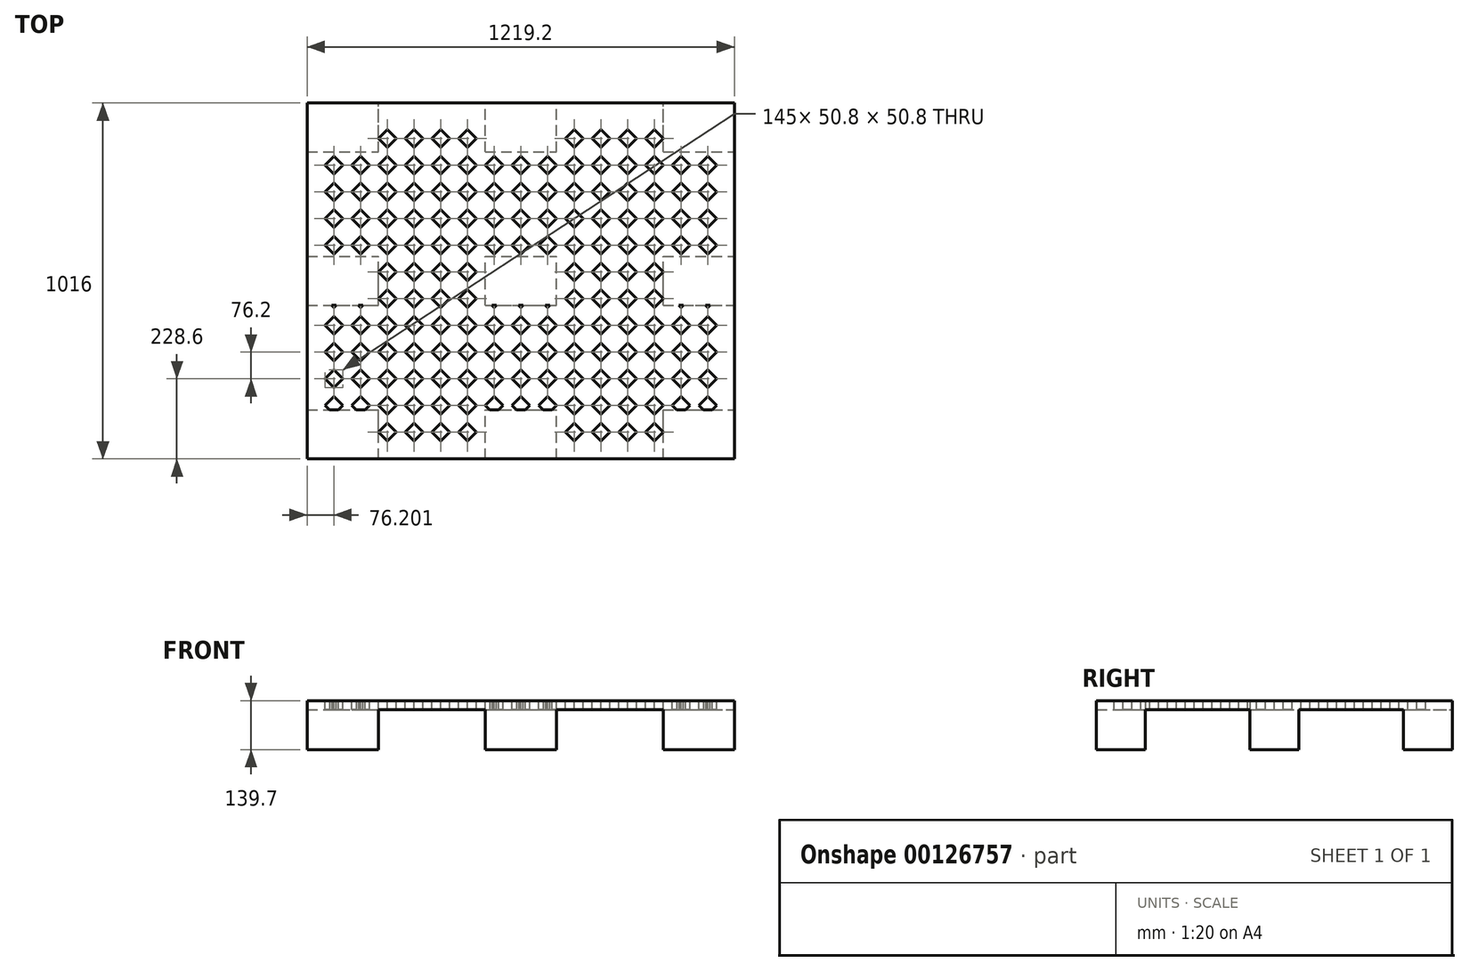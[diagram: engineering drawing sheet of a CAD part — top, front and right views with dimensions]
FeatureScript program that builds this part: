
annotation { "Feature Type Name" : "Feature", "Feature Type Description" : "" }
export const myFeature = defineFeature(function(context is Context, id is Id, definition is map)
    precondition{}
    {
        {
            var Q0;
            Q0=qCreatedBy(makeId("Top.planeOp"),FACE);
            var sketch = newSketch(context, id + "F0", { "sketchPlane" : qUnion([Q0])});
            skLineSegment(sketch, "E0.bottom", {"start": v(643.63, 508) * mm, "end": v(-575.57, 508) * mm});
            skLineSegment(sketch, "E0.top", {"start": v(643.63, -508) * mm, "end": v(-575.57, -508) * mm});
            skLineSegment(sketch, "E0.left", {"start": v(643.63, 508) * mm, "end": v(643.63, -508) * mm});
            skLineSegment(sketch, "E0.right", {"start": v(-575.57, 508) * mm, "end": v(-575.57, -508) * mm});
            skPoint(sketch, "E0.middle", {"position": v(34.03, 0) * mm});
            skSolve(sketch);
        }
        {
            var Q0;
            Q0 = qSketchRegion(id + "F0", true);
            extrude(context, id + "F1", {"entities" : qUnion([Q0]), "depth" : 25.4 * mm});
        }
        {
            var Q0;
            Q0=makeQuery(id+"F1.opExtrude","CAP_FACE",FACE,{"disambiguationData":[OSD([sQuery(id+"F0.wireOp",EDGE,"E0.bottom"),sQuery(id+"F0.wireOp",EDGE,"E0.top"),sQuery(id+"F0.wireOp",EDGE,"E0.left"),sQuery(id+"F0.wireOp",EDGE,"E0.right")])],"isStart":false});
            var sketch = newSketch(context, id + "F2", { "sketchPlane" : qUnion([Q0])});
            skLineSegment(sketch, "E1.bottom", {"start": v(-575.57, -508) * mm, "end": v(-524.77, -508) * mm, "construction": true});
            skLineSegment(sketch, "E1.top", {"start": v(-575.57, -457.2) * mm, "end": v(-524.77, -457.2) * mm, "construction": true});
            skLineSegment(sketch, "E1.left", {"start": v(-575.57, -508) * mm, "end": v(-575.57, -457.2) * mm, "construction": true});
            skLineSegment(sketch, "E1.right", {"start": v(-524.77, -508) * mm, "end": v(-524.77, -457.2) * mm, "construction": true});
            skLineSegment(sketch, "E2.bottom", {"start": v(-524.77, -457.2) * mm, "end": v(-473.97, -457.2) * mm, "construction": true});
            skLineSegment(sketch, "E2.top", {"start": v(-524.77, -406.4) * mm, "end": v(-473.97, -406.4) * mm, "construction": true});
            skLineSegment(sketch, "E2.left", {"start": v(-524.77, -457.2) * mm, "end": v(-524.77, -406.4) * mm, "construction": true});
            skLineSegment(sketch, "E2.right", {"start": v(-473.97, -457.2) * mm, "end": v(-473.97, -406.4) * mm, "construction": true});
            skLineSegment(sketch, "E3", {"start": v(-524.77, -431.8) * mm, "end": v(-499.37, -406.4) * mm});
            skLineSegment(sketch, "E4", {"start": v(-499.37, -406.4) * mm, "end": v(-473.97, -431.8) * mm});
            skLineSegment(sketch, "E5", {"start": v(-473.97, -431.8) * mm, "end": v(-499.37, -457.2) * mm});
            skLineSegment(sketch, "E6", {"start": v(-499.37, -457.2) * mm, "end": v(-524.77, -431.8) * mm});
            skLineSegment(sketch, "E7.0.1.0", {"start": v(-499.37, -330.2) * mm, "end": v(-473.97, -355.6) * mm});
            skLineSegment(sketch, "E7.0.1.1", {"start": v(-524.77, -355.6) * mm, "end": v(-499.37, -330.2) * mm});
            skLineSegment(sketch, "E7.0.1.2", {"start": v(-499.37, -381) * mm, "end": v(-524.77, -355.6) * mm});
            skLineSegment(sketch, "E7.0.1.3", {"start": v(-473.97, -355.6) * mm, "end": v(-499.37, -381) * mm});
            skLineSegment(sketch, "E7.0.2.0", {"start": v(-499.37, -254) * mm, "end": v(-473.97, -279.4) * mm});
            skLineSegment(sketch, "E7.0.2.1", {"start": v(-524.77, -279.4) * mm, "end": v(-499.37, -254) * mm});
            skLineSegment(sketch, "E7.0.2.2", {"start": v(-499.37, -304.8) * mm, "end": v(-524.77, -279.4) * mm});
            skLineSegment(sketch, "E7.0.2.3", {"start": v(-473.97, -279.4) * mm, "end": v(-499.37, -304.8) * mm});
            skLineSegment(sketch, "E7.0.3.0", {"start": v(-499.37, -177.8) * mm, "end": v(-473.97, -203.2) * mm});
            skLineSegment(sketch, "E7.0.3.1", {"start": v(-524.77, -203.2) * mm, "end": v(-499.37, -177.8) * mm});
            skLineSegment(sketch, "E7.0.3.2", {"start": v(-499.37, -228.6) * mm, "end": v(-524.77, -203.2) * mm});
            skLineSegment(sketch, "E7.0.3.3", {"start": v(-473.97, -203.2) * mm, "end": v(-499.37, -228.6) * mm});
            skLineSegment(sketch, "E7.0.4.0", {"start": v(-499.37, -101.6) * mm, "end": v(-473.97, -127) * mm});
            skLineSegment(sketch, "E7.0.4.1", {"start": v(-524.77, -127) * mm, "end": v(-499.37, -101.6) * mm});
            skLineSegment(sketch, "E7.0.4.2", {"start": v(-499.37, -152.4) * mm, "end": v(-524.77, -127) * mm});
            skLineSegment(sketch, "E7.0.4.3", {"start": v(-473.97, -127) * mm, "end": v(-499.37, -152.4) * mm});
            skLineSegment(sketch, "E7.0.5.0", {"start": v(-499.37, -25.4) * mm, "end": v(-473.97, -50.8) * mm});
            skLineSegment(sketch, "E7.0.5.1", {"start": v(-524.77, -50.8) * mm, "end": v(-499.37, -25.4) * mm});
            skLineSegment(sketch, "E7.0.5.2", {"start": v(-499.37, -76.2) * mm, "end": v(-524.77, -50.8) * mm});
            skLineSegment(sketch, "E7.0.5.3", {"start": v(-473.97, -50.8) * mm, "end": v(-499.37, -76.2) * mm});
            skLineSegment(sketch, "E7.0.6.0", {"start": v(-499.37, 50.8) * mm, "end": v(-473.97, 25.4) * mm});
            skLineSegment(sketch, "E7.0.6.1", {"start": v(-524.77, 25.4) * mm, "end": v(-499.37, 50.8) * mm});
            skLineSegment(sketch, "E7.0.6.2", {"start": v(-499.37, 0) * mm, "end": v(-524.77, 25.4) * mm});
            skLineSegment(sketch, "E7.0.6.3", {"start": v(-473.97, 25.4) * mm, "end": v(-499.37, 0) * mm});
            skLineSegment(sketch, "E7.0.7.0", {"start": v(-499.37, 127) * mm, "end": v(-473.97, 101.6) * mm});
            skLineSegment(sketch, "E7.0.7.1", {"start": v(-524.77, 101.6) * mm, "end": v(-499.37, 127) * mm});
            skLineSegment(sketch, "E7.0.7.2", {"start": v(-499.37, 76.2) * mm, "end": v(-524.77, 101.6) * mm});
            skLineSegment(sketch, "E7.0.7.3", {"start": v(-473.97, 101.6) * mm, "end": v(-499.37, 76.2) * mm});
            skLineSegment(sketch, "E7.0.8.0", {"start": v(-499.37, 203.2) * mm, "end": v(-473.97, 177.8) * mm});
            skLineSegment(sketch, "E7.0.8.1", {"start": v(-524.77, 177.8) * mm, "end": v(-499.37, 203.2) * mm});
            skLineSegment(sketch, "E7.0.8.2", {"start": v(-499.37, 152.4) * mm, "end": v(-524.77, 177.8) * mm});
            skLineSegment(sketch, "E7.0.8.3", {"start": v(-473.97, 177.8) * mm, "end": v(-499.37, 152.4) * mm});
            skLineSegment(sketch, "E7.0.9.0", {"start": v(-499.37, 279.4) * mm, "end": v(-473.97, 254) * mm});
            skLineSegment(sketch, "E7.0.9.1", {"start": v(-524.77, 254) * mm, "end": v(-499.37, 279.4) * mm});
            skLineSegment(sketch, "E7.0.9.2", {"start": v(-499.37, 228.6) * mm, "end": v(-524.77, 254) * mm});
            skLineSegment(sketch, "E7.0.9.3", {"start": v(-473.97, 254) * mm, "end": v(-499.37, 228.6) * mm});
            skLineSegment(sketch, "E7.0.10.0", {"start": v(-499.37, 355.6) * mm, "end": v(-473.97, 330.2) * mm});
            skLineSegment(sketch, "E7.0.10.1", {"start": v(-524.77, 330.2) * mm, "end": v(-499.37, 355.6) * mm});
            skLineSegment(sketch, "E7.0.10.2", {"start": v(-499.37, 304.8) * mm, "end": v(-524.77, 330.2) * mm});
            skLineSegment(sketch, "E7.0.10.3", {"start": v(-473.97, 330.2) * mm, "end": v(-499.37, 304.8) * mm});
            skLineSegment(sketch, "E7.0.11.0", {"start": v(-499.37, 431.8) * mm, "end": v(-473.97, 406.4) * mm});
            skLineSegment(sketch, "E7.0.11.1", {"start": v(-524.77, 406.4) * mm, "end": v(-499.37, 431.8) * mm});
            skLineSegment(sketch, "E7.0.11.2", {"start": v(-499.37, 381) * mm, "end": v(-524.77, 406.4) * mm});
            skLineSegment(sketch, "E7.0.11.3", {"start": v(-473.97, 406.4) * mm, "end": v(-499.37, 381) * mm});
            skLineSegment(sketch, "E7.1.0.0", {"start": v(-423.17, -406.4) * mm, "end": v(-397.77, -431.8) * mm});
            skLineSegment(sketch, "E7.1.0.1", {"start": v(-448.57, -431.8) * mm, "end": v(-423.17, -406.4) * mm});
            skLineSegment(sketch, "E7.1.0.2", {"start": v(-423.17, -457.2) * mm, "end": v(-448.57, -431.8) * mm});
            skLineSegment(sketch, "E7.1.0.3", {"start": v(-397.77, -431.8) * mm, "end": v(-423.17, -457.2) * mm});
            skLineSegment(sketch, "E7.1.1.0", {"start": v(-423.17, -330.2) * mm, "end": v(-397.77, -355.6) * mm});
            skLineSegment(sketch, "E7.1.1.1", {"start": v(-448.57, -355.6) * mm, "end": v(-423.17, -330.2) * mm});
            skLineSegment(sketch, "E7.1.1.2", {"start": v(-423.17, -381) * mm, "end": v(-448.57, -355.6) * mm});
            skLineSegment(sketch, "E7.1.1.3", {"start": v(-397.77, -355.6) * mm, "end": v(-423.17, -381) * mm});
            skLineSegment(sketch, "E7.1.2.0", {"start": v(-423.17, -254) * mm, "end": v(-397.77, -279.4) * mm});
            skLineSegment(sketch, "E7.1.2.1", {"start": v(-448.57, -279.4) * mm, "end": v(-423.17, -254) * mm});
            skLineSegment(sketch, "E7.1.2.2", {"start": v(-423.17, -304.8) * mm, "end": v(-448.57, -279.4) * mm});
            skLineSegment(sketch, "E7.1.2.3", {"start": v(-397.77, -279.4) * mm, "end": v(-423.17, -304.8) * mm});
            skLineSegment(sketch, "E7.1.3.0", {"start": v(-423.17, -177.8) * mm, "end": v(-397.77, -203.2) * mm});
            skLineSegment(sketch, "E7.1.3.1", {"start": v(-448.57, -203.2) * mm, "end": v(-423.17, -177.8) * mm});
            skLineSegment(sketch, "E7.1.3.2", {"start": v(-423.17, -228.6) * mm, "end": v(-448.57, -203.2) * mm});
            skLineSegment(sketch, "E7.1.3.3", {"start": v(-397.77, -203.2) * mm, "end": v(-423.17, -228.6) * mm});
            skLineSegment(sketch, "E7.1.4.0", {"start": v(-423.17, -101.6) * mm, "end": v(-397.77, -127) * mm});
            skLineSegment(sketch, "E7.1.4.1", {"start": v(-448.57, -127) * mm, "end": v(-423.17, -101.6) * mm});
            skLineSegment(sketch, "E7.1.4.2", {"start": v(-423.17, -152.4) * mm, "end": v(-448.57, -127) * mm});
            skLineSegment(sketch, "E7.1.4.3", {"start": v(-397.77, -127) * mm, "end": v(-423.17, -152.4) * mm});
            skLineSegment(sketch, "E7.1.5.0", {"start": v(-423.17, -25.4) * mm, "end": v(-397.77, -50.8) * mm});
            skLineSegment(sketch, "E7.1.5.1", {"start": v(-448.57, -50.8) * mm, "end": v(-423.17, -25.4) * mm});
            skLineSegment(sketch, "E7.1.5.2", {"start": v(-423.17, -76.2) * mm, "end": v(-448.57, -50.8) * mm});
            skLineSegment(sketch, "E7.1.5.3", {"start": v(-397.77, -50.8) * mm, "end": v(-423.17, -76.2) * mm});
            skLineSegment(sketch, "E7.1.6.0", {"start": v(-423.17, 50.8) * mm, "end": v(-397.77, 25.4) * mm});
            skLineSegment(sketch, "E7.1.6.1", {"start": v(-448.57, 25.4) * mm, "end": v(-423.17, 50.8) * mm});
            skLineSegment(sketch, "E7.1.6.2", {"start": v(-423.17, 0) * mm, "end": v(-448.57, 25.4) * mm});
            skLineSegment(sketch, "E7.1.6.3", {"start": v(-397.77, 25.4) * mm, "end": v(-423.17, 0) * mm});
            skLineSegment(sketch, "E7.1.7.0", {"start": v(-423.17, 127) * mm, "end": v(-397.77, 101.6) * mm});
            skLineSegment(sketch, "E7.1.7.1", {"start": v(-448.57, 101.6) * mm, "end": v(-423.17, 127) * mm});
            skLineSegment(sketch, "E7.1.7.2", {"start": v(-423.17, 76.2) * mm, "end": v(-448.57, 101.6) * mm});
            skLineSegment(sketch, "E7.1.7.3", {"start": v(-397.77, 101.6) * mm, "end": v(-423.17, 76.2) * mm});
            skLineSegment(sketch, "E7.1.8.0", {"start": v(-423.17, 203.2) * mm, "end": v(-397.77, 177.8) * mm});
            skLineSegment(sketch, "E7.1.8.1", {"start": v(-448.57, 177.8) * mm, "end": v(-423.17, 203.2) * mm});
            skLineSegment(sketch, "E7.1.8.2", {"start": v(-423.17, 152.4) * mm, "end": v(-448.57, 177.8) * mm});
            skLineSegment(sketch, "E7.1.8.3", {"start": v(-397.77, 177.8) * mm, "end": v(-423.17, 152.4) * mm});
            skLineSegment(sketch, "E7.1.9.0", {"start": v(-423.17, 279.4) * mm, "end": v(-397.77, 254) * mm});
            skLineSegment(sketch, "E7.1.9.1", {"start": v(-448.57, 254) * mm, "end": v(-423.17, 279.4) * mm});
            skLineSegment(sketch, "E7.1.9.2", {"start": v(-423.17, 228.6) * mm, "end": v(-448.57, 254) * mm});
            skLineSegment(sketch, "E7.1.9.3", {"start": v(-397.77, 254) * mm, "end": v(-423.17, 228.6) * mm});
            skLineSegment(sketch, "E7.1.10.0", {"start": v(-423.17, 355.6) * mm, "end": v(-397.77, 330.2) * mm});
            skLineSegment(sketch, "E7.1.10.1", {"start": v(-448.57, 330.2) * mm, "end": v(-423.17, 355.6) * mm});
            skLineSegment(sketch, "E7.1.10.2", {"start": v(-423.17, 304.8) * mm, "end": v(-448.57, 330.2) * mm});
            skLineSegment(sketch, "E7.1.10.3", {"start": v(-397.77, 330.2) * mm, "end": v(-423.17, 304.8) * mm});
            skLineSegment(sketch, "E7.1.11.0", {"start": v(-423.17, 431.8) * mm, "end": v(-397.77, 406.4) * mm});
            skLineSegment(sketch, "E7.1.11.1", {"start": v(-448.57, 406.4) * mm, "end": v(-423.17, 431.8) * mm});
            skLineSegment(sketch, "E7.1.11.2", {"start": v(-423.17, 381) * mm, "end": v(-448.57, 406.4) * mm});
            skLineSegment(sketch, "E7.1.11.3", {"start": v(-397.77, 406.4) * mm, "end": v(-423.17, 381) * mm});
            skLineSegment(sketch, "E7.2.0.0", {"start": v(-346.97, -406.4) * mm, "end": v(-321.57, -431.8) * mm});
            skLineSegment(sketch, "E7.2.0.1", {"start": v(-372.37, -431.8) * mm, "end": v(-346.97, -406.4) * mm});
            skLineSegment(sketch, "E7.2.0.2", {"start": v(-346.97, -457.2) * mm, "end": v(-372.37, -431.8) * mm});
            skLineSegment(sketch, "E7.2.0.3", {"start": v(-321.57, -431.8) * mm, "end": v(-346.97, -457.2) * mm});
            skLineSegment(sketch, "E7.2.1.0", {"start": v(-346.97, -330.2) * mm, "end": v(-321.57, -355.6) * mm});
            skLineSegment(sketch, "E7.2.1.1", {"start": v(-372.37, -355.6) * mm, "end": v(-346.97, -330.2) * mm});
            skLineSegment(sketch, "E7.2.1.2", {"start": v(-346.97, -381) * mm, "end": v(-372.37, -355.6) * mm});
            skLineSegment(sketch, "E7.2.1.3", {"start": v(-321.57, -355.6) * mm, "end": v(-346.97, -381) * mm});
            skLineSegment(sketch, "E7.2.2.0", {"start": v(-346.97, -254) * mm, "end": v(-321.57, -279.4) * mm});
            skLineSegment(sketch, "E7.2.2.1", {"start": v(-372.37, -279.4) * mm, "end": v(-346.97, -254) * mm});
            skLineSegment(sketch, "E7.2.2.2", {"start": v(-346.97, -304.8) * mm, "end": v(-372.37, -279.4) * mm});
            skLineSegment(sketch, "E7.2.2.3", {"start": v(-321.57, -279.4) * mm, "end": v(-346.97, -304.8) * mm});
            skLineSegment(sketch, "E7.2.3.0", {"start": v(-346.97, -177.8) * mm, "end": v(-321.57, -203.2) * mm});
            skLineSegment(sketch, "E7.2.3.1", {"start": v(-372.37, -203.2) * mm, "end": v(-346.97, -177.8) * mm});
            skLineSegment(sketch, "E7.2.3.2", {"start": v(-346.97, -228.6) * mm, "end": v(-372.37, -203.2) * mm});
            skLineSegment(sketch, "E7.2.3.3", {"start": v(-321.57, -203.2) * mm, "end": v(-346.97, -228.6) * mm});
            skLineSegment(sketch, "E7.2.4.0", {"start": v(-346.97, -101.6) * mm, "end": v(-321.57, -127) * mm});
            skLineSegment(sketch, "E7.2.4.1", {"start": v(-372.37, -127) * mm, "end": v(-346.97, -101.6) * mm});
            skLineSegment(sketch, "E7.2.4.2", {"start": v(-346.97, -152.4) * mm, "end": v(-372.37, -127) * mm});
            skLineSegment(sketch, "E7.2.4.3", {"start": v(-321.57, -127) * mm, "end": v(-346.97, -152.4) * mm});
            skLineSegment(sketch, "E7.2.5.0", {"start": v(-346.97, -25.4) * mm, "end": v(-321.57, -50.8) * mm});
            skLineSegment(sketch, "E7.2.5.1", {"start": v(-372.37, -50.8) * mm, "end": v(-346.97, -25.4) * mm});
            skLineSegment(sketch, "E7.2.5.2", {"start": v(-346.97, -76.2) * mm, "end": v(-372.37, -50.8) * mm});
            skLineSegment(sketch, "E7.2.5.3", {"start": v(-321.57, -50.8) * mm, "end": v(-346.97, -76.2) * mm});
            skLineSegment(sketch, "E7.2.6.0", {"start": v(-346.97, 50.8) * mm, "end": v(-321.57, 25.4) * mm});
            skLineSegment(sketch, "E7.2.6.1", {"start": v(-372.37, 25.4) * mm, "end": v(-346.97, 50.8) * mm});
            skLineSegment(sketch, "E7.2.6.2", {"start": v(-346.97, 0) * mm, "end": v(-372.37, 25.4) * mm});
            skLineSegment(sketch, "E7.2.6.3", {"start": v(-321.57, 25.4) * mm, "end": v(-346.97, 0) * mm});
            skLineSegment(sketch, "E7.2.7.0", {"start": v(-346.97, 127) * mm, "end": v(-321.57, 101.6) * mm});
            skLineSegment(sketch, "E7.2.7.1", {"start": v(-372.37, 101.6) * mm, "end": v(-346.97, 127) * mm});
            skLineSegment(sketch, "E7.2.7.2", {"start": v(-346.97, 76.2) * mm, "end": v(-372.37, 101.6) * mm});
            skLineSegment(sketch, "E7.2.7.3", {"start": v(-321.57, 101.6) * mm, "end": v(-346.97, 76.2) * mm});
            skLineSegment(sketch, "E7.2.8.0", {"start": v(-346.97, 203.2) * mm, "end": v(-321.57, 177.8) * mm});
            skLineSegment(sketch, "E7.2.8.1", {"start": v(-372.37, 177.8) * mm, "end": v(-346.97, 203.2) * mm});
            skLineSegment(sketch, "E7.2.8.2", {"start": v(-346.97, 152.4) * mm, "end": v(-372.37, 177.8) * mm});
            skLineSegment(sketch, "E7.2.8.3", {"start": v(-321.57, 177.8) * mm, "end": v(-346.97, 152.4) * mm});
            skLineSegment(sketch, "E7.2.9.0", {"start": v(-346.97, 279.4) * mm, "end": v(-321.57, 254) * mm});
            skLineSegment(sketch, "E7.2.9.1", {"start": v(-372.37, 254) * mm, "end": v(-346.97, 279.4) * mm});
            skLineSegment(sketch, "E7.2.9.2", {"start": v(-346.97, 228.6) * mm, "end": v(-372.37, 254) * mm});
            skLineSegment(sketch, "E7.2.9.3", {"start": v(-321.57, 254) * mm, "end": v(-346.97, 228.6) * mm});
            skLineSegment(sketch, "E7.2.10.0", {"start": v(-346.97, 355.6) * mm, "end": v(-321.57, 330.2) * mm});
            skLineSegment(sketch, "E7.2.10.1", {"start": v(-372.37, 330.2) * mm, "end": v(-346.97, 355.6) * mm});
            skLineSegment(sketch, "E7.2.10.2", {"start": v(-346.97, 304.8) * mm, "end": v(-372.37, 330.2) * mm});
            skLineSegment(sketch, "E7.2.10.3", {"start": v(-321.57, 330.2) * mm, "end": v(-346.97, 304.8) * mm});
            skLineSegment(sketch, "E7.2.11.0", {"start": v(-346.97, 431.8) * mm, "end": v(-321.57, 406.4) * mm});
            skLineSegment(sketch, "E7.2.11.1", {"start": v(-372.37, 406.4) * mm, "end": v(-346.97, 431.8) * mm});
            skLineSegment(sketch, "E7.2.11.2", {"start": v(-346.97, 381) * mm, "end": v(-372.37, 406.4) * mm});
            skLineSegment(sketch, "E7.2.11.3", {"start": v(-321.57, 406.4) * mm, "end": v(-346.97, 381) * mm});
            skLineSegment(sketch, "E7.3.0.0", {"start": v(-270.77, -406.4) * mm, "end": v(-245.37, -431.8) * mm});
            skLineSegment(sketch, "E7.3.0.1", {"start": v(-296.17, -431.8) * mm, "end": v(-270.77, -406.4) * mm});
            skLineSegment(sketch, "E7.3.0.2", {"start": v(-270.77, -457.2) * mm, "end": v(-296.17, -431.8) * mm});
            skLineSegment(sketch, "E7.3.0.3", {"start": v(-245.37, -431.8) * mm, "end": v(-270.77, -457.2) * mm});
            skLineSegment(sketch, "E7.3.1.0", {"start": v(-270.77, -330.2) * mm, "end": v(-245.37, -355.6) * mm});
            skLineSegment(sketch, "E7.3.1.1", {"start": v(-296.17, -355.6) * mm, "end": v(-270.77, -330.2) * mm});
            skLineSegment(sketch, "E7.3.1.2", {"start": v(-270.77, -381) * mm, "end": v(-296.17, -355.6) * mm});
            skLineSegment(sketch, "E7.3.1.3", {"start": v(-245.37, -355.6) * mm, "end": v(-270.77, -381) * mm});
            skLineSegment(sketch, "E7.3.2.0", {"start": v(-270.77, -254) * mm, "end": v(-245.37, -279.4) * mm});
            skLineSegment(sketch, "E7.3.2.1", {"start": v(-296.17, -279.4) * mm, "end": v(-270.77, -254) * mm});
            skLineSegment(sketch, "E7.3.2.2", {"start": v(-270.77, -304.8) * mm, "end": v(-296.17, -279.4) * mm});
            skLineSegment(sketch, "E7.3.2.3", {"start": v(-245.37, -279.4) * mm, "end": v(-270.77, -304.8) * mm});
            skLineSegment(sketch, "E7.3.3.0", {"start": v(-270.77, -177.8) * mm, "end": v(-245.37, -203.2) * mm});
            skLineSegment(sketch, "E7.3.3.1", {"start": v(-296.17, -203.2) * mm, "end": v(-270.77, -177.8) * mm});
            skLineSegment(sketch, "E7.3.3.2", {"start": v(-270.77, -228.6) * mm, "end": v(-296.17, -203.2) * mm});
            skLineSegment(sketch, "E7.3.3.3", {"start": v(-245.37, -203.2) * mm, "end": v(-270.77, -228.6) * mm});
            skLineSegment(sketch, "E7.3.4.0", {"start": v(-270.77, -101.6) * mm, "end": v(-245.37, -127) * mm});
            skLineSegment(sketch, "E7.3.4.1", {"start": v(-296.17, -127) * mm, "end": v(-270.77, -101.6) * mm});
            skLineSegment(sketch, "E7.3.4.2", {"start": v(-270.77, -152.4) * mm, "end": v(-296.17, -127) * mm});
            skLineSegment(sketch, "E7.3.4.3", {"start": v(-245.37, -127) * mm, "end": v(-270.77, -152.4) * mm});
            skLineSegment(sketch, "E7.3.5.0", {"start": v(-270.77, -25.4) * mm, "end": v(-245.37, -50.8) * mm});
            skLineSegment(sketch, "E7.3.5.1", {"start": v(-296.17, -50.8) * mm, "end": v(-270.77, -25.4) * mm});
            skLineSegment(sketch, "E7.3.5.2", {"start": v(-270.77, -76.2) * mm, "end": v(-296.17, -50.8) * mm});
            skLineSegment(sketch, "E7.3.5.3", {"start": v(-245.37, -50.8) * mm, "end": v(-270.77, -76.2) * mm});
            skLineSegment(sketch, "E7.3.6.0", {"start": v(-270.77, 50.8) * mm, "end": v(-245.37, 25.4) * mm});
            skLineSegment(sketch, "E7.3.6.1", {"start": v(-296.17, 25.4) * mm, "end": v(-270.77, 50.8) * mm});
            skLineSegment(sketch, "E7.3.6.2", {"start": v(-270.77, 0) * mm, "end": v(-296.17, 25.4) * mm});
            skLineSegment(sketch, "E7.3.6.3", {"start": v(-245.37, 25.4) * mm, "end": v(-270.77, 0) * mm});
            skLineSegment(sketch, "E7.3.7.0", {"start": v(-270.77, 127) * mm, "end": v(-245.37, 101.6) * mm});
            skLineSegment(sketch, "E7.3.7.1", {"start": v(-296.17, 101.6) * mm, "end": v(-270.77, 127) * mm});
            skLineSegment(sketch, "E7.3.7.2", {"start": v(-270.77, 76.2) * mm, "end": v(-296.17, 101.6) * mm});
            skLineSegment(sketch, "E7.3.7.3", {"start": v(-245.37, 101.6) * mm, "end": v(-270.77, 76.2) * mm});
            skLineSegment(sketch, "E7.3.8.0", {"start": v(-270.77, 203.2) * mm, "end": v(-245.37, 177.8) * mm});
            skLineSegment(sketch, "E7.3.8.1", {"start": v(-296.17, 177.8) * mm, "end": v(-270.77, 203.2) * mm});
            skLineSegment(sketch, "E7.3.8.2", {"start": v(-270.77, 152.4) * mm, "end": v(-296.17, 177.8) * mm});
            skLineSegment(sketch, "E7.3.8.3", {"start": v(-245.37, 177.8) * mm, "end": v(-270.77, 152.4) * mm});
            skLineSegment(sketch, "E7.3.9.0", {"start": v(-270.77, 279.4) * mm, "end": v(-245.37, 254) * mm});
            skLineSegment(sketch, "E7.3.9.1", {"start": v(-296.17, 254) * mm, "end": v(-270.77, 279.4) * mm});
            skLineSegment(sketch, "E7.3.9.2", {"start": v(-270.77, 228.6) * mm, "end": v(-296.17, 254) * mm});
            skLineSegment(sketch, "E7.3.9.3", {"start": v(-245.37, 254) * mm, "end": v(-270.77, 228.6) * mm});
            skLineSegment(sketch, "E7.3.10.0", {"start": v(-270.77, 355.6) * mm, "end": v(-245.37, 330.2) * mm});
            skLineSegment(sketch, "E7.3.10.1", {"start": v(-296.17, 330.2) * mm, "end": v(-270.77, 355.6) * mm});
            skLineSegment(sketch, "E7.3.10.2", {"start": v(-270.77, 304.8) * mm, "end": v(-296.17, 330.2) * mm});
            skLineSegment(sketch, "E7.3.10.3", {"start": v(-245.37, 330.2) * mm, "end": v(-270.77, 304.8) * mm});
            skLineSegment(sketch, "E7.3.11.0", {"start": v(-270.77, 431.8) * mm, "end": v(-245.37, 406.4) * mm});
            skLineSegment(sketch, "E7.3.11.1", {"start": v(-296.17, 406.4) * mm, "end": v(-270.77, 431.8) * mm});
            skLineSegment(sketch, "E7.3.11.2", {"start": v(-270.77, 381) * mm, "end": v(-296.17, 406.4) * mm});
            skLineSegment(sketch, "E7.3.11.3", {"start": v(-245.37, 406.4) * mm, "end": v(-270.77, 381) * mm});
            skLineSegment(sketch, "E7.4.0.0", {"start": v(-194.57, -406.4) * mm, "end": v(-169.17, -431.8) * mm});
            skLineSegment(sketch, "E7.4.0.1", {"start": v(-219.97, -431.8) * mm, "end": v(-194.57, -406.4) * mm});
            skLineSegment(sketch, "E7.4.0.2", {"start": v(-194.57, -457.2) * mm, "end": v(-219.97, -431.8) * mm});
            skLineSegment(sketch, "E7.4.0.3", {"start": v(-169.17, -431.8) * mm, "end": v(-194.57, -457.2) * mm});
            skLineSegment(sketch, "E7.4.1.0", {"start": v(-194.57, -330.2) * mm, "end": v(-169.17, -355.6) * mm});
            skLineSegment(sketch, "E7.4.1.1", {"start": v(-219.97, -355.6) * mm, "end": v(-194.57, -330.2) * mm});
            skLineSegment(sketch, "E7.4.1.2", {"start": v(-194.57, -381) * mm, "end": v(-219.97, -355.6) * mm});
            skLineSegment(sketch, "E7.4.1.3", {"start": v(-169.17, -355.6) * mm, "end": v(-194.57, -381) * mm});
            skLineSegment(sketch, "E7.4.2.0", {"start": v(-194.57, -254) * mm, "end": v(-169.17, -279.4) * mm});
            skLineSegment(sketch, "E7.4.2.1", {"start": v(-219.97, -279.4) * mm, "end": v(-194.57, -254) * mm});
            skLineSegment(sketch, "E7.4.2.2", {"start": v(-194.57, -304.8) * mm, "end": v(-219.97, -279.4) * mm});
            skLineSegment(sketch, "E7.4.2.3", {"start": v(-169.17, -279.4) * mm, "end": v(-194.57, -304.8) * mm});
            skLineSegment(sketch, "E7.4.3.0", {"start": v(-194.57, -177.8) * mm, "end": v(-169.17, -203.2) * mm});
            skLineSegment(sketch, "E7.4.3.1", {"start": v(-219.97, -203.2) * mm, "end": v(-194.57, -177.8) * mm});
            skLineSegment(sketch, "E7.4.3.2", {"start": v(-194.57, -228.6) * mm, "end": v(-219.97, -203.2) * mm});
            skLineSegment(sketch, "E7.4.3.3", {"start": v(-169.17, -203.2) * mm, "end": v(-194.57, -228.6) * mm});
            skLineSegment(sketch, "E7.4.4.0", {"start": v(-194.57, -101.6) * mm, "end": v(-169.17, -127) * mm});
            skLineSegment(sketch, "E7.4.4.1", {"start": v(-219.97, -127) * mm, "end": v(-194.57, -101.6) * mm});
            skLineSegment(sketch, "E7.4.4.2", {"start": v(-194.57, -152.4) * mm, "end": v(-219.97, -127) * mm});
            skLineSegment(sketch, "E7.4.4.3", {"start": v(-169.17, -127) * mm, "end": v(-194.57, -152.4) * mm});
            skLineSegment(sketch, "E7.4.5.0", {"start": v(-194.57, -25.4) * mm, "end": v(-169.17, -50.8) * mm});
            skLineSegment(sketch, "E7.4.5.1", {"start": v(-219.97, -50.8) * mm, "end": v(-194.57, -25.4) * mm});
            skLineSegment(sketch, "E7.4.5.2", {"start": v(-194.57, -76.2) * mm, "end": v(-219.97, -50.8) * mm});
            skLineSegment(sketch, "E7.4.5.3", {"start": v(-169.17, -50.8) * mm, "end": v(-194.57, -76.2) * mm});
            skLineSegment(sketch, "E7.4.6.0", {"start": v(-194.57, 50.8) * mm, "end": v(-169.17, 25.4) * mm});
            skLineSegment(sketch, "E7.4.6.1", {"start": v(-219.97, 25.4) * mm, "end": v(-194.57, 50.8) * mm});
            skLineSegment(sketch, "E7.4.6.2", {"start": v(-194.57, 0) * mm, "end": v(-219.97, 25.4) * mm});
            skLineSegment(sketch, "E7.4.6.3", {"start": v(-169.17, 25.4) * mm, "end": v(-194.57, 0) * mm});
            skLineSegment(sketch, "E7.4.7.0", {"start": v(-194.57, 127) * mm, "end": v(-169.17, 101.6) * mm});
            skLineSegment(sketch, "E7.4.7.1", {"start": v(-219.97, 101.6) * mm, "end": v(-194.57, 127) * mm});
            skLineSegment(sketch, "E7.4.7.2", {"start": v(-194.57, 76.2) * mm, "end": v(-219.97, 101.6) * mm});
            skLineSegment(sketch, "E7.4.7.3", {"start": v(-169.17, 101.6) * mm, "end": v(-194.57, 76.2) * mm});
            skLineSegment(sketch, "E7.4.8.0", {"start": v(-194.57, 203.2) * mm, "end": v(-169.17, 177.8) * mm});
            skLineSegment(sketch, "E7.4.8.1", {"start": v(-219.97, 177.8) * mm, "end": v(-194.57, 203.2) * mm});
            skLineSegment(sketch, "E7.4.8.2", {"start": v(-194.57, 152.4) * mm, "end": v(-219.97, 177.8) * mm});
            skLineSegment(sketch, "E7.4.8.3", {"start": v(-169.17, 177.8) * mm, "end": v(-194.57, 152.4) * mm});
            skLineSegment(sketch, "E7.4.9.0", {"start": v(-194.57, 279.4) * mm, "end": v(-169.17, 254) * mm});
            skLineSegment(sketch, "E7.4.9.1", {"start": v(-219.97, 254) * mm, "end": v(-194.57, 279.4) * mm});
            skLineSegment(sketch, "E7.4.9.2", {"start": v(-194.57, 228.6) * mm, "end": v(-219.97, 254) * mm});
            skLineSegment(sketch, "E7.4.9.3", {"start": v(-169.17, 254) * mm, "end": v(-194.57, 228.6) * mm});
            skLineSegment(sketch, "E7.4.10.0", {"start": v(-194.57, 355.6) * mm, "end": v(-169.17, 330.2) * mm});
            skLineSegment(sketch, "E7.4.10.1", {"start": v(-219.97, 330.2) * mm, "end": v(-194.57, 355.6) * mm});
            skLineSegment(sketch, "E7.4.10.2", {"start": v(-194.57, 304.8) * mm, "end": v(-219.97, 330.2) * mm});
            skLineSegment(sketch, "E7.4.10.3", {"start": v(-169.17, 330.2) * mm, "end": v(-194.57, 304.8) * mm});
            skLineSegment(sketch, "E7.4.11.0", {"start": v(-194.57, 431.8) * mm, "end": v(-169.17, 406.4) * mm});
            skLineSegment(sketch, "E7.4.11.1", {"start": v(-219.97, 406.4) * mm, "end": v(-194.57, 431.8) * mm});
            skLineSegment(sketch, "E7.4.11.2", {"start": v(-194.57, 381) * mm, "end": v(-219.97, 406.4) * mm});
            skLineSegment(sketch, "E7.4.11.3", {"start": v(-169.17, 406.4) * mm, "end": v(-194.57, 381) * mm});
            skLineSegment(sketch, "E7.5.0.0", {"start": v(-118.37, -406.4) * mm, "end": v(-92.97, -431.8) * mm});
            skLineSegment(sketch, "E7.5.0.1", {"start": v(-143.77, -431.8) * mm, "end": v(-118.37, -406.4) * mm});
            skLineSegment(sketch, "E7.5.0.2", {"start": v(-118.37, -457.2) * mm, "end": v(-143.77, -431.8) * mm});
            skLineSegment(sketch, "E7.5.0.3", {"start": v(-92.97, -431.8) * mm, "end": v(-118.37, -457.2) * mm});
            skLineSegment(sketch, "E7.5.1.0", {"start": v(-118.37, -330.2) * mm, "end": v(-92.97, -355.6) * mm});
            skLineSegment(sketch, "E7.5.1.1", {"start": v(-143.77, -355.6) * mm, "end": v(-118.37, -330.2) * mm});
            skLineSegment(sketch, "E7.5.1.2", {"start": v(-118.37, -381) * mm, "end": v(-143.77, -355.6) * mm});
            skLineSegment(sketch, "E7.5.1.3", {"start": v(-92.97, -355.6) * mm, "end": v(-118.37, -381) * mm});
            skLineSegment(sketch, "E7.5.2.0", {"start": v(-118.37, -254) * mm, "end": v(-92.97, -279.4) * mm});
            skLineSegment(sketch, "E7.5.2.1", {"start": v(-143.77, -279.4) * mm, "end": v(-118.37, -254) * mm});
            skLineSegment(sketch, "E7.5.2.2", {"start": v(-118.37, -304.8) * mm, "end": v(-143.77, -279.4) * mm});
            skLineSegment(sketch, "E7.5.2.3", {"start": v(-92.97, -279.4) * mm, "end": v(-118.37, -304.8) * mm});
            skLineSegment(sketch, "E7.5.3.0", {"start": v(-118.37, -177.8) * mm, "end": v(-92.97, -203.2) * mm});
            skLineSegment(sketch, "E7.5.3.1", {"start": v(-143.77, -203.2) * mm, "end": v(-118.37, -177.8) * mm});
            skLineSegment(sketch, "E7.5.3.2", {"start": v(-118.37, -228.6) * mm, "end": v(-143.77, -203.2) * mm});
            skLineSegment(sketch, "E7.5.3.3", {"start": v(-92.97, -203.2) * mm, "end": v(-118.37, -228.6) * mm});
            skLineSegment(sketch, "E7.5.4.0", {"start": v(-118.37, -101.6) * mm, "end": v(-92.97, -127) * mm});
            skLineSegment(sketch, "E7.5.4.1", {"start": v(-143.77, -127) * mm, "end": v(-118.37, -101.6) * mm});
            skLineSegment(sketch, "E7.5.4.2", {"start": v(-118.37, -152.4) * mm, "end": v(-143.77, -127) * mm});
            skLineSegment(sketch, "E7.5.4.3", {"start": v(-92.97, -127) * mm, "end": v(-118.37, -152.4) * mm});
            skLineSegment(sketch, "E7.5.5.0", {"start": v(-118.37, -25.4) * mm, "end": v(-92.97, -50.8) * mm});
            skLineSegment(sketch, "E7.5.5.1", {"start": v(-143.77, -50.8) * mm, "end": v(-118.37, -25.4) * mm});
            skLineSegment(sketch, "E7.5.5.2", {"start": v(-118.37, -76.2) * mm, "end": v(-143.77, -50.8) * mm});
            skLineSegment(sketch, "E7.5.5.3", {"start": v(-92.97, -50.8) * mm, "end": v(-118.37, -76.2) * mm});
            skLineSegment(sketch, "E7.5.6.0", {"start": v(-118.37, 50.8) * mm, "end": v(-92.97, 25.4) * mm});
            skLineSegment(sketch, "E7.5.6.1", {"start": v(-143.77, 25.4) * mm, "end": v(-118.37, 50.8) * mm});
            skLineSegment(sketch, "E7.5.6.2", {"start": v(-118.37, 0) * mm, "end": v(-143.77, 25.4) * mm});
            skLineSegment(sketch, "E7.5.6.3", {"start": v(-92.97, 25.4) * mm, "end": v(-118.37, 0) * mm});
            skLineSegment(sketch, "E7.5.7.0", {"start": v(-118.37, 127) * mm, "end": v(-92.97, 101.6) * mm});
            skLineSegment(sketch, "E7.5.7.1", {"start": v(-143.77, 101.6) * mm, "end": v(-118.37, 127) * mm});
            skLineSegment(sketch, "E7.5.7.2", {"start": v(-118.37, 76.2) * mm, "end": v(-143.77, 101.6) * mm});
            skLineSegment(sketch, "E7.5.7.3", {"start": v(-92.97, 101.6) * mm, "end": v(-118.37, 76.2) * mm});
            skLineSegment(sketch, "E7.5.8.0", {"start": v(-118.37, 203.2) * mm, "end": v(-92.97, 177.8) * mm});
            skLineSegment(sketch, "E7.5.8.1", {"start": v(-143.77, 177.8) * mm, "end": v(-118.37, 203.2) * mm});
            skLineSegment(sketch, "E7.5.8.2", {"start": v(-118.37, 152.4) * mm, "end": v(-143.77, 177.8) * mm});
            skLineSegment(sketch, "E7.5.8.3", {"start": v(-92.97, 177.8) * mm, "end": v(-118.37, 152.4) * mm});
            skLineSegment(sketch, "E7.5.9.0", {"start": v(-118.37, 279.4) * mm, "end": v(-92.97, 254) * mm});
            skLineSegment(sketch, "E7.5.9.1", {"start": v(-143.77, 254) * mm, "end": v(-118.37, 279.4) * mm});
            skLineSegment(sketch, "E7.5.9.2", {"start": v(-118.37, 228.6) * mm, "end": v(-143.77, 254) * mm});
            skLineSegment(sketch, "E7.5.9.3", {"start": v(-92.97, 254) * mm, "end": v(-118.37, 228.6) * mm});
            skLineSegment(sketch, "E7.5.10.0", {"start": v(-118.37, 355.6) * mm, "end": v(-92.97, 330.2) * mm});
            skLineSegment(sketch, "E7.5.10.1", {"start": v(-143.77, 330.2) * mm, "end": v(-118.37, 355.6) * mm});
            skLineSegment(sketch, "E7.5.10.2", {"start": v(-118.37, 304.8) * mm, "end": v(-143.77, 330.2) * mm});
            skLineSegment(sketch, "E7.5.10.3", {"start": v(-92.97, 330.2) * mm, "end": v(-118.37, 304.8) * mm});
            skLineSegment(sketch, "E7.5.11.0", {"start": v(-118.37, 431.8) * mm, "end": v(-92.97, 406.4) * mm});
            skLineSegment(sketch, "E7.5.11.1", {"start": v(-143.77, 406.4) * mm, "end": v(-118.37, 431.8) * mm});
            skLineSegment(sketch, "E7.5.11.2", {"start": v(-118.37, 381) * mm, "end": v(-143.77, 406.4) * mm});
            skLineSegment(sketch, "E7.5.11.3", {"start": v(-92.97, 406.4) * mm, "end": v(-118.37, 381) * mm});
            skLineSegment(sketch, "E7.6.0.0", {"start": v(-42.17, -406.4) * mm, "end": v(-16.77, -431.8) * mm});
            skLineSegment(sketch, "E7.6.0.1", {"start": v(-67.57, -431.8) * mm, "end": v(-42.17, -406.4) * mm});
            skLineSegment(sketch, "E7.6.0.2", {"start": v(-42.17, -457.2) * mm, "end": v(-67.57, -431.8) * mm});
            skLineSegment(sketch, "E7.6.0.3", {"start": v(-16.77, -431.8) * mm, "end": v(-42.17, -457.2) * mm});
            skLineSegment(sketch, "E7.6.1.0", {"start": v(-42.17, -330.2) * mm, "end": v(-16.77, -355.6) * mm});
            skLineSegment(sketch, "E7.6.1.1", {"start": v(-67.57, -355.6) * mm, "end": v(-42.17, -330.2) * mm});
            skLineSegment(sketch, "E7.6.1.2", {"start": v(-42.17, -381) * mm, "end": v(-67.57, -355.6) * mm});
            skLineSegment(sketch, "E7.6.1.3", {"start": v(-16.77, -355.6) * mm, "end": v(-42.17, -381) * mm});
            skLineSegment(sketch, "E7.6.2.0", {"start": v(-42.17, -254) * mm, "end": v(-16.77, -279.4) * mm});
            skLineSegment(sketch, "E7.6.2.1", {"start": v(-67.57, -279.4) * mm, "end": v(-42.17, -254) * mm});
            skLineSegment(sketch, "E7.6.2.2", {"start": v(-42.17, -304.8) * mm, "end": v(-67.57, -279.4) * mm});
            skLineSegment(sketch, "E7.6.2.3", {"start": v(-16.77, -279.4) * mm, "end": v(-42.17, -304.8) * mm});
            skLineSegment(sketch, "E7.6.3.0", {"start": v(-42.17, -177.8) * mm, "end": v(-16.77, -203.2) * mm});
            skLineSegment(sketch, "E7.6.3.1", {"start": v(-67.57, -203.2) * mm, "end": v(-42.17, -177.8) * mm});
            skLineSegment(sketch, "E7.6.3.2", {"start": v(-42.17, -228.6) * mm, "end": v(-67.57, -203.2) * mm});
            skLineSegment(sketch, "E7.6.3.3", {"start": v(-16.77, -203.2) * mm, "end": v(-42.17, -228.6) * mm});
            skLineSegment(sketch, "E7.6.4.0", {"start": v(-42.17, -101.6) * mm, "end": v(-16.77, -127) * mm});
            skLineSegment(sketch, "E7.6.4.1", {"start": v(-67.57, -127) * mm, "end": v(-42.17, -101.6) * mm});
            skLineSegment(sketch, "E7.6.4.2", {"start": v(-42.17, -152.4) * mm, "end": v(-67.57, -127) * mm});
            skLineSegment(sketch, "E7.6.4.3", {"start": v(-16.77, -127) * mm, "end": v(-42.17, -152.4) * mm});
            skLineSegment(sketch, "E7.6.5.0", {"start": v(-42.17, -25.4) * mm, "end": v(-16.77, -50.8) * mm});
            skLineSegment(sketch, "E7.6.5.1", {"start": v(-67.57, -50.8) * mm, "end": v(-42.17, -25.4) * mm});
            skLineSegment(sketch, "E7.6.5.2", {"start": v(-42.17, -76.2) * mm, "end": v(-67.57, -50.8) * mm});
            skLineSegment(sketch, "E7.6.5.3", {"start": v(-16.77, -50.8) * mm, "end": v(-42.17, -76.2) * mm});
            skLineSegment(sketch, "E7.6.6.0", {"start": v(-42.17, 50.8) * mm, "end": v(-16.77, 25.4) * mm});
            skLineSegment(sketch, "E7.6.6.1", {"start": v(-67.57, 25.4) * mm, "end": v(-42.17, 50.8) * mm});
            skLineSegment(sketch, "E7.6.6.2", {"start": v(-42.17, 0) * mm, "end": v(-67.57, 25.4) * mm});
            skLineSegment(sketch, "E7.6.6.3", {"start": v(-16.77, 25.4) * mm, "end": v(-42.17, 0) * mm});
            skLineSegment(sketch, "E7.6.7.0", {"start": v(-42.17, 127) * mm, "end": v(-16.77, 101.6) * mm});
            skLineSegment(sketch, "E7.6.7.1", {"start": v(-67.57, 101.6) * mm, "end": v(-42.17, 127) * mm});
            skLineSegment(sketch, "E7.6.7.2", {"start": v(-42.17, 76.2) * mm, "end": v(-67.57, 101.6) * mm});
            skLineSegment(sketch, "E7.6.7.3", {"start": v(-16.77, 101.6) * mm, "end": v(-42.17, 76.2) * mm});
            skLineSegment(sketch, "E7.6.8.0", {"start": v(-42.17, 203.2) * mm, "end": v(-16.77, 177.8) * mm});
            skLineSegment(sketch, "E7.6.8.1", {"start": v(-67.57, 177.8) * mm, "end": v(-42.17, 203.2) * mm});
            skLineSegment(sketch, "E7.6.8.2", {"start": v(-42.17, 152.4) * mm, "end": v(-67.57, 177.8) * mm});
            skLineSegment(sketch, "E7.6.8.3", {"start": v(-16.77, 177.8) * mm, "end": v(-42.17, 152.4) * mm});
            skLineSegment(sketch, "E7.6.9.0", {"start": v(-42.17, 279.4) * mm, "end": v(-16.77, 254) * mm});
            skLineSegment(sketch, "E7.6.9.1", {"start": v(-67.57, 254) * mm, "end": v(-42.17, 279.4) * mm});
            skLineSegment(sketch, "E7.6.9.2", {"start": v(-42.17, 228.6) * mm, "end": v(-67.57, 254) * mm});
            skLineSegment(sketch, "E7.6.9.3", {"start": v(-16.77, 254) * mm, "end": v(-42.17, 228.6) * mm});
            skLineSegment(sketch, "E7.6.10.0", {"start": v(-42.17, 355.6) * mm, "end": v(-16.77, 330.2) * mm});
            skLineSegment(sketch, "E7.6.10.1", {"start": v(-67.57, 330.2) * mm, "end": v(-42.17, 355.6) * mm});
            skLineSegment(sketch, "E7.6.10.2", {"start": v(-42.17, 304.8) * mm, "end": v(-67.57, 330.2) * mm});
            skLineSegment(sketch, "E7.6.10.3", {"start": v(-16.77, 330.2) * mm, "end": v(-42.17, 304.8) * mm});
            skLineSegment(sketch, "E7.6.11.0", {"start": v(-42.17, 431.8) * mm, "end": v(-16.77, 406.4) * mm});
            skLineSegment(sketch, "E7.6.11.1", {"start": v(-67.57, 406.4) * mm, "end": v(-42.17, 431.8) * mm});
            skLineSegment(sketch, "E7.6.11.2", {"start": v(-42.17, 381) * mm, "end": v(-67.57, 406.4) * mm});
            skLineSegment(sketch, "E7.6.11.3", {"start": v(-16.77, 406.4) * mm, "end": v(-42.17, 381) * mm});
            skLineSegment(sketch, "E7.7.0.0", {"start": v(34.03, -406.4) * mm, "end": v(59.43, -431.8) * mm});
            skLineSegment(sketch, "E7.7.0.1", {"start": v(8.63, -431.8) * mm, "end": v(34.03, -406.4) * mm});
            skLineSegment(sketch, "E7.7.0.2", {"start": v(34.03, -457.2) * mm, "end": v(8.63, -431.8) * mm});
            skLineSegment(sketch, "E7.7.0.3", {"start": v(59.43, -431.8) * mm, "end": v(34.03, -457.2) * mm});
            skLineSegment(sketch, "E7.7.1.0", {"start": v(34.03, -330.2) * mm, "end": v(59.43, -355.6) * mm});
            skLineSegment(sketch, "E7.7.1.1", {"start": v(8.63, -355.6) * mm, "end": v(34.03, -330.2) * mm});
            skLineSegment(sketch, "E7.7.1.2", {"start": v(34.03, -381) * mm, "end": v(8.63, -355.6) * mm});
            skLineSegment(sketch, "E7.7.1.3", {"start": v(59.43, -355.6) * mm, "end": v(34.03, -381) * mm});
            skLineSegment(sketch, "E7.7.2.0", {"start": v(34.03, -254) * mm, "end": v(59.43, -279.4) * mm});
            skLineSegment(sketch, "E7.7.2.1", {"start": v(8.63, -279.4) * mm, "end": v(34.03, -254) * mm});
            skLineSegment(sketch, "E7.7.2.2", {"start": v(34.03, -304.8) * mm, "end": v(8.63, -279.4) * mm});
            skLineSegment(sketch, "E7.7.2.3", {"start": v(59.43, -279.4) * mm, "end": v(34.03, -304.8) * mm});
            skLineSegment(sketch, "E7.7.3.0", {"start": v(34.03, -177.8) * mm, "end": v(59.43, -203.2) * mm});
            skLineSegment(sketch, "E7.7.3.1", {"start": v(8.63, -203.2) * mm, "end": v(34.03, -177.8) * mm});
            skLineSegment(sketch, "E7.7.3.2", {"start": v(34.03, -228.6) * mm, "end": v(8.63, -203.2) * mm});
            skLineSegment(sketch, "E7.7.3.3", {"start": v(59.43, -203.2) * mm, "end": v(34.03, -228.6) * mm});
            skLineSegment(sketch, "E7.7.4.0", {"start": v(34.03, -101.6) * mm, "end": v(59.43, -127) * mm});
            skLineSegment(sketch, "E7.7.4.1", {"start": v(8.63, -127) * mm, "end": v(34.03, -101.6) * mm});
            skLineSegment(sketch, "E7.7.4.2", {"start": v(34.03, -152.4) * mm, "end": v(8.63, -127) * mm});
            skLineSegment(sketch, "E7.7.4.3", {"start": v(59.43, -127) * mm, "end": v(34.03, -152.4) * mm});
            skLineSegment(sketch, "E7.7.5.0", {"start": v(34.03, -25.4) * mm, "end": v(59.43, -50.8) * mm});
            skLineSegment(sketch, "E7.7.5.1", {"start": v(8.63, -50.8) * mm, "end": v(34.03, -25.4) * mm});
            skLineSegment(sketch, "E7.7.5.2", {"start": v(34.03, -76.2) * mm, "end": v(8.63, -50.8) * mm});
            skLineSegment(sketch, "E7.7.5.3", {"start": v(59.43, -50.8) * mm, "end": v(34.03, -76.2) * mm});
            skLineSegment(sketch, "E7.7.6.0", {"start": v(34.03, 50.8) * mm, "end": v(59.43, 25.4) * mm});
            skLineSegment(sketch, "E7.7.6.1", {"start": v(8.63, 25.4) * mm, "end": v(34.03, 50.8) * mm});
            skLineSegment(sketch, "E7.7.6.2", {"start": v(34.03, 0) * mm, "end": v(8.63, 25.4) * mm});
            skLineSegment(sketch, "E7.7.6.3", {"start": v(59.43, 25.4) * mm, "end": v(34.03, 0) * mm});
            skLineSegment(sketch, "E7.7.7.0", {"start": v(34.03, 127) * mm, "end": v(59.43, 101.6) * mm});
            skLineSegment(sketch, "E7.7.7.1", {"start": v(8.63, 101.6) * mm, "end": v(34.03, 127) * mm});
            skLineSegment(sketch, "E7.7.7.2", {"start": v(34.03, 76.2) * mm, "end": v(8.63, 101.6) * mm});
            skLineSegment(sketch, "E7.7.7.3", {"start": v(59.43, 101.6) * mm, "end": v(34.03, 76.2) * mm});
            skLineSegment(sketch, "E7.7.8.0", {"start": v(34.03, 203.2) * mm, "end": v(59.43, 177.8) * mm});
            skLineSegment(sketch, "E7.7.8.1", {"start": v(8.63, 177.8) * mm, "end": v(34.03, 203.2) * mm});
            skLineSegment(sketch, "E7.7.8.2", {"start": v(34.03, 152.4) * mm, "end": v(8.63, 177.8) * mm});
            skLineSegment(sketch, "E7.7.8.3", {"start": v(59.43, 177.8) * mm, "end": v(34.03, 152.4) * mm});
            skLineSegment(sketch, "E7.7.9.0", {"start": v(34.03, 279.4) * mm, "end": v(59.43, 254) * mm});
            skLineSegment(sketch, "E7.7.9.1", {"start": v(8.63, 254) * mm, "end": v(34.03, 279.4) * mm});
            skLineSegment(sketch, "E7.7.9.2", {"start": v(34.03, 228.6) * mm, "end": v(8.63, 254) * mm});
            skLineSegment(sketch, "E7.7.9.3", {"start": v(59.43, 254) * mm, "end": v(34.03, 228.6) * mm});
            skLineSegment(sketch, "E7.7.10.0", {"start": v(34.03, 355.6) * mm, "end": v(59.43, 330.2) * mm});
            skLineSegment(sketch, "E7.7.10.1", {"start": v(8.63, 330.2) * mm, "end": v(34.03, 355.6) * mm});
            skLineSegment(sketch, "E7.7.10.2", {"start": v(34.03, 304.8) * mm, "end": v(8.63, 330.2) * mm});
            skLineSegment(sketch, "E7.7.10.3", {"start": v(59.43, 330.2) * mm, "end": v(34.03, 304.8) * mm});
            skLineSegment(sketch, "E7.7.11.0", {"start": v(34.03, 431.8) * mm, "end": v(59.43, 406.4) * mm});
            skLineSegment(sketch, "E7.7.11.1", {"start": v(8.63, 406.4) * mm, "end": v(34.03, 431.8) * mm});
            skLineSegment(sketch, "E7.7.11.2", {"start": v(34.03, 381) * mm, "end": v(8.63, 406.4) * mm});
            skLineSegment(sketch, "E7.7.11.3", {"start": v(59.43, 406.4) * mm, "end": v(34.03, 381) * mm});
            skLineSegment(sketch, "E7.8.0.0", {"start": v(110.23, -406.4) * mm, "end": v(135.63, -431.8) * mm});
            skLineSegment(sketch, "E7.8.0.1", {"start": v(84.83, -431.8) * mm, "end": v(110.23, -406.4) * mm});
            skLineSegment(sketch, "E7.8.0.2", {"start": v(110.23, -457.2) * mm, "end": v(84.83, -431.8) * mm});
            skLineSegment(sketch, "E7.8.0.3", {"start": v(135.63, -431.8) * mm, "end": v(110.23, -457.2) * mm});
            skLineSegment(sketch, "E7.8.1.0", {"start": v(110.23, -330.2) * mm, "end": v(135.63, -355.6) * mm});
            skLineSegment(sketch, "E7.8.1.1", {"start": v(84.83, -355.6) * mm, "end": v(110.23, -330.2) * mm});
            skLineSegment(sketch, "E7.8.1.2", {"start": v(110.23, -381) * mm, "end": v(84.83, -355.6) * mm});
            skLineSegment(sketch, "E7.8.1.3", {"start": v(135.63, -355.6) * mm, "end": v(110.23, -381) * mm});
            skLineSegment(sketch, "E7.8.2.0", {"start": v(110.23, -254) * mm, "end": v(135.63, -279.4) * mm});
            skLineSegment(sketch, "E7.8.2.1", {"start": v(84.83, -279.4) * mm, "end": v(110.23, -254) * mm});
            skLineSegment(sketch, "E7.8.2.2", {"start": v(110.23, -304.8) * mm, "end": v(84.83, -279.4) * mm});
            skLineSegment(sketch, "E7.8.2.3", {"start": v(135.63, -279.4) * mm, "end": v(110.23, -304.8) * mm});
            skLineSegment(sketch, "E7.8.3.0", {"start": v(110.23, -177.8) * mm, "end": v(135.63, -203.2) * mm});
            skLineSegment(sketch, "E7.8.3.1", {"start": v(84.83, -203.2) * mm, "end": v(110.23, -177.8) * mm});
            skLineSegment(sketch, "E7.8.3.2", {"start": v(110.23, -228.6) * mm, "end": v(84.83, -203.2) * mm});
            skLineSegment(sketch, "E7.8.3.3", {"start": v(135.63, -203.2) * mm, "end": v(110.23, -228.6) * mm});
            skLineSegment(sketch, "E7.8.4.0", {"start": v(110.23, -101.6) * mm, "end": v(135.63, -127) * mm});
            skLineSegment(sketch, "E7.8.4.1", {"start": v(84.83, -127) * mm, "end": v(110.23, -101.6) * mm});
            skLineSegment(sketch, "E7.8.4.2", {"start": v(110.23, -152.4) * mm, "end": v(84.83, -127) * mm});
            skLineSegment(sketch, "E7.8.4.3", {"start": v(135.63, -127) * mm, "end": v(110.23, -152.4) * mm});
            skLineSegment(sketch, "E7.8.5.0", {"start": v(110.23, -25.4) * mm, "end": v(135.63, -50.8) * mm});
            skLineSegment(sketch, "E7.8.5.1", {"start": v(84.83, -50.8) * mm, "end": v(110.23, -25.4) * mm});
            skLineSegment(sketch, "E7.8.5.2", {"start": v(110.23, -76.2) * mm, "end": v(84.83, -50.8) * mm});
            skLineSegment(sketch, "E7.8.5.3", {"start": v(135.63, -50.8) * mm, "end": v(110.23, -76.2) * mm});
            skLineSegment(sketch, "E7.8.6.0", {"start": v(110.23, 50.8) * mm, "end": v(135.63, 25.4) * mm});
            skLineSegment(sketch, "E7.8.6.1", {"start": v(84.83, 25.4) * mm, "end": v(110.23, 50.8) * mm});
            skLineSegment(sketch, "E7.8.6.2", {"start": v(110.23, 0) * mm, "end": v(84.83, 25.4) * mm});
            skLineSegment(sketch, "E7.8.6.3", {"start": v(135.63, 25.4) * mm, "end": v(110.23, 0) * mm});
            skLineSegment(sketch, "E7.8.7.0", {"start": v(110.23, 127) * mm, "end": v(135.63, 101.6) * mm});
            skLineSegment(sketch, "E7.8.7.1", {"start": v(84.83, 101.6) * mm, "end": v(110.23, 127) * mm});
            skLineSegment(sketch, "E7.8.7.2", {"start": v(110.23, 76.2) * mm, "end": v(84.83, 101.6) * mm});
            skLineSegment(sketch, "E7.8.7.3", {"start": v(135.63, 101.6) * mm, "end": v(110.23, 76.2) * mm});
            skLineSegment(sketch, "E7.8.8.0", {"start": v(110.23, 203.2) * mm, "end": v(135.63, 177.8) * mm});
            skLineSegment(sketch, "E7.8.8.1", {"start": v(84.83, 177.8) * mm, "end": v(110.23, 203.2) * mm});
            skLineSegment(sketch, "E7.8.8.2", {"start": v(110.23, 152.4) * mm, "end": v(84.83, 177.8) * mm});
            skLineSegment(sketch, "E7.8.8.3", {"start": v(135.63, 177.8) * mm, "end": v(110.23, 152.4) * mm});
            skLineSegment(sketch, "E7.8.9.0", {"start": v(110.23, 279.4) * mm, "end": v(135.63, 254) * mm});
            skLineSegment(sketch, "E7.8.9.1", {"start": v(84.83, 254) * mm, "end": v(110.23, 279.4) * mm});
            skLineSegment(sketch, "E7.8.9.2", {"start": v(110.23, 228.6) * mm, "end": v(84.83, 254) * mm});
            skLineSegment(sketch, "E7.8.9.3", {"start": v(135.63, 254) * mm, "end": v(110.23, 228.6) * mm});
            skLineSegment(sketch, "E7.8.10.0", {"start": v(110.23, 355.6) * mm, "end": v(135.63, 330.2) * mm});
            skLineSegment(sketch, "E7.8.10.1", {"start": v(84.83, 330.2) * mm, "end": v(110.23, 355.6) * mm});
            skLineSegment(sketch, "E7.8.10.2", {"start": v(110.23, 304.8) * mm, "end": v(84.83, 330.2) * mm});
            skLineSegment(sketch, "E7.8.10.3", {"start": v(135.63, 330.2) * mm, "end": v(110.23, 304.8) * mm});
            skLineSegment(sketch, "E7.8.11.0", {"start": v(110.23, 431.8) * mm, "end": v(135.63, 406.4) * mm});
            skLineSegment(sketch, "E7.8.11.1", {"start": v(84.83, 406.4) * mm, "end": v(110.23, 431.8) * mm});
            skLineSegment(sketch, "E7.8.11.2", {"start": v(110.23, 381) * mm, "end": v(84.83, 406.4) * mm});
            skLineSegment(sketch, "E7.8.11.3", {"start": v(135.63, 406.4) * mm, "end": v(110.23, 381) * mm});
            skLineSegment(sketch, "E7.9.0.0", {"start": v(186.43, -406.4) * mm, "end": v(211.83, -431.8) * mm});
            skLineSegment(sketch, "E7.9.0.1", {"start": v(161.03, -431.8) * mm, "end": v(186.43, -406.4) * mm});
            skLineSegment(sketch, "E7.9.0.2", {"start": v(186.43, -457.2) * mm, "end": v(161.03, -431.8) * mm});
            skLineSegment(sketch, "E7.9.0.3", {"start": v(211.83, -431.8) * mm, "end": v(186.43, -457.2) * mm});
            skLineSegment(sketch, "E7.9.1.0", {"start": v(186.43, -330.2) * mm, "end": v(211.83, -355.6) * mm});
            skLineSegment(sketch, "E7.9.1.1", {"start": v(161.03, -355.6) * mm, "end": v(186.43, -330.2) * mm});
            skLineSegment(sketch, "E7.9.1.2", {"start": v(186.43, -381) * mm, "end": v(161.03, -355.6) * mm});
            skLineSegment(sketch, "E7.9.1.3", {"start": v(211.83, -355.6) * mm, "end": v(186.43, -381) * mm});
            skLineSegment(sketch, "E7.9.2.0", {"start": v(186.43, -254) * mm, "end": v(211.83, -279.4) * mm});
            skLineSegment(sketch, "E7.9.2.1", {"start": v(161.03, -279.4) * mm, "end": v(186.43, -254) * mm});
            skLineSegment(sketch, "E7.9.2.2", {"start": v(186.43, -304.8) * mm, "end": v(161.03, -279.4) * mm});
            skLineSegment(sketch, "E7.9.2.3", {"start": v(211.83, -279.4) * mm, "end": v(186.43, -304.8) * mm});
            skLineSegment(sketch, "E7.9.3.0", {"start": v(186.43, -177.8) * mm, "end": v(211.83, -203.2) * mm});
            skLineSegment(sketch, "E7.9.3.1", {"start": v(161.03, -203.2) * mm, "end": v(186.43, -177.8) * mm});
            skLineSegment(sketch, "E7.9.3.2", {"start": v(186.43, -228.6) * mm, "end": v(161.03, -203.2) * mm});
            skLineSegment(sketch, "E7.9.3.3", {"start": v(211.83, -203.2) * mm, "end": v(186.43, -228.6) * mm});
            skLineSegment(sketch, "E7.9.4.0", {"start": v(186.43, -101.6) * mm, "end": v(211.83, -127) * mm});
            skLineSegment(sketch, "E7.9.4.1", {"start": v(161.03, -127) * mm, "end": v(186.43, -101.6) * mm});
            skLineSegment(sketch, "E7.9.4.2", {"start": v(186.43, -152.4) * mm, "end": v(161.03, -127) * mm});
            skLineSegment(sketch, "E7.9.4.3", {"start": v(211.83, -127) * mm, "end": v(186.43, -152.4) * mm});
            skLineSegment(sketch, "E7.9.5.0", {"start": v(186.43, -25.4) * mm, "end": v(211.83, -50.8) * mm});
            skLineSegment(sketch, "E7.9.5.1", {"start": v(161.03, -50.8) * mm, "end": v(186.43, -25.4) * mm});
            skLineSegment(sketch, "E7.9.5.2", {"start": v(186.43, -76.2) * mm, "end": v(161.03, -50.8) * mm});
            skLineSegment(sketch, "E7.9.5.3", {"start": v(211.83, -50.8) * mm, "end": v(186.43, -76.2) * mm});
            skLineSegment(sketch, "E7.9.6.0", {"start": v(186.43, 50.8) * mm, "end": v(211.83, 25.4) * mm});
            skLineSegment(sketch, "E7.9.6.1", {"start": v(161.03, 25.4) * mm, "end": v(186.43, 50.8) * mm});
            skLineSegment(sketch, "E7.9.6.2", {"start": v(186.43, 0) * mm, "end": v(161.03, 25.4) * mm});
            skLineSegment(sketch, "E7.9.6.3", {"start": v(211.83, 25.4) * mm, "end": v(186.43, 0) * mm});
            skLineSegment(sketch, "E7.9.7.0", {"start": v(186.43, 127) * mm, "end": v(211.83, 101.6) * mm});
            skLineSegment(sketch, "E7.9.7.1", {"start": v(161.03, 101.6) * mm, "end": v(186.43, 127) * mm});
            skLineSegment(sketch, "E7.9.7.2", {"start": v(186.43, 76.2) * mm, "end": v(161.03, 101.6) * mm});
            skLineSegment(sketch, "E7.9.7.3", {"start": v(211.83, 101.6) * mm, "end": v(186.43, 76.2) * mm});
            skLineSegment(sketch, "E7.9.8.0", {"start": v(186.43, 203.2) * mm, "end": v(211.83, 177.8) * mm});
            skLineSegment(sketch, "E7.9.8.1", {"start": v(161.03, 177.8) * mm, "end": v(186.43, 203.2) * mm});
            skLineSegment(sketch, "E7.9.8.2", {"start": v(186.43, 152.4) * mm, "end": v(161.03, 177.8) * mm});
            skLineSegment(sketch, "E7.9.8.3", {"start": v(211.83, 177.8) * mm, "end": v(186.43, 152.4) * mm});
            skLineSegment(sketch, "E7.9.9.0", {"start": v(186.43, 279.4) * mm, "end": v(211.83, 254) * mm});
            skLineSegment(sketch, "E7.9.9.1", {"start": v(161.03, 254) * mm, "end": v(186.43, 279.4) * mm});
            skLineSegment(sketch, "E7.9.9.2", {"start": v(186.43, 228.6) * mm, "end": v(161.03, 254) * mm});
            skLineSegment(sketch, "E7.9.9.3", {"start": v(211.83, 254) * mm, "end": v(186.43, 228.6) * mm});
            skLineSegment(sketch, "E7.9.10.0", {"start": v(186.43, 355.6) * mm, "end": v(211.83, 330.2) * mm});
            skLineSegment(sketch, "E7.9.10.1", {"start": v(161.03, 330.2) * mm, "end": v(186.43, 355.6) * mm});
            skLineSegment(sketch, "E7.9.10.2", {"start": v(186.43, 304.8) * mm, "end": v(161.03, 330.2) * mm});
            skLineSegment(sketch, "E7.9.10.3", {"start": v(211.83, 330.2) * mm, "end": v(186.43, 304.8) * mm});
            skLineSegment(sketch, "E7.9.11.0", {"start": v(186.43, 431.8) * mm, "end": v(211.83, 406.4) * mm});
            skLineSegment(sketch, "E7.9.11.1", {"start": v(161.03, 406.4) * mm, "end": v(186.43, 431.8) * mm});
            skLineSegment(sketch, "E7.9.11.2", {"start": v(186.43, 381) * mm, "end": v(161.03, 406.4) * mm});
            skLineSegment(sketch, "E7.9.11.3", {"start": v(211.83, 406.4) * mm, "end": v(186.43, 381) * mm});
            skLineSegment(sketch, "E7.10.0.0", {"start": v(262.63, -406.4) * mm, "end": v(288.03, -431.8) * mm});
            skLineSegment(sketch, "E7.10.0.1", {"start": v(237.23, -431.8) * mm, "end": v(262.63, -406.4) * mm});
            skLineSegment(sketch, "E7.10.0.2", {"start": v(262.63, -457.2) * mm, "end": v(237.23, -431.8) * mm});
            skLineSegment(sketch, "E7.10.0.3", {"start": v(288.03, -431.8) * mm, "end": v(262.63, -457.2) * mm});
            skLineSegment(sketch, "E7.10.1.0", {"start": v(262.63, -330.2) * mm, "end": v(288.03, -355.6) * mm});
            skLineSegment(sketch, "E7.10.1.1", {"start": v(237.23, -355.6) * mm, "end": v(262.63, -330.2) * mm});
            skLineSegment(sketch, "E7.10.1.2", {"start": v(262.63, -381) * mm, "end": v(237.23, -355.6) * mm});
            skLineSegment(sketch, "E7.10.1.3", {"start": v(288.03, -355.6) * mm, "end": v(262.63, -381) * mm});
            skLineSegment(sketch, "E7.10.2.0", {"start": v(262.63, -254) * mm, "end": v(288.03, -279.4) * mm});
            skLineSegment(sketch, "E7.10.2.1", {"start": v(237.23, -279.4) * mm, "end": v(262.63, -254) * mm});
            skLineSegment(sketch, "E7.10.2.2", {"start": v(262.63, -304.8) * mm, "end": v(237.23, -279.4) * mm});
            skLineSegment(sketch, "E7.10.2.3", {"start": v(288.03, -279.4) * mm, "end": v(262.63, -304.8) * mm});
            skLineSegment(sketch, "E7.10.3.0", {"start": v(262.63, -177.8) * mm, "end": v(288.03, -203.2) * mm});
            skLineSegment(sketch, "E7.10.3.1", {"start": v(237.23, -203.2) * mm, "end": v(262.63, -177.8) * mm});
            skLineSegment(sketch, "E7.10.3.2", {"start": v(262.63, -228.6) * mm, "end": v(237.23, -203.2) * mm});
            skLineSegment(sketch, "E7.10.3.3", {"start": v(288.03, -203.2) * mm, "end": v(262.63, -228.6) * mm});
            skLineSegment(sketch, "E7.10.4.0", {"start": v(262.63, -101.6) * mm, "end": v(288.03, -127) * mm});
            skLineSegment(sketch, "E7.10.4.1", {"start": v(237.23, -127) * mm, "end": v(262.63, -101.6) * mm});
            skLineSegment(sketch, "E7.10.4.2", {"start": v(262.63, -152.4) * mm, "end": v(237.23, -127) * mm});
            skLineSegment(sketch, "E7.10.4.3", {"start": v(288.03, -127) * mm, "end": v(262.63, -152.4) * mm});
            skLineSegment(sketch, "E7.10.5.0", {"start": v(262.63, -25.4) * mm, "end": v(288.03, -50.8) * mm});
            skLineSegment(sketch, "E7.10.5.1", {"start": v(237.23, -50.8) * mm, "end": v(262.63, -25.4) * mm});
            skLineSegment(sketch, "E7.10.5.2", {"start": v(262.63, -76.2) * mm, "end": v(237.23, -50.8) * mm});
            skLineSegment(sketch, "E7.10.5.3", {"start": v(288.03, -50.8) * mm, "end": v(262.63, -76.2) * mm});
            skLineSegment(sketch, "E7.10.6.0", {"start": v(262.63, 50.8) * mm, "end": v(288.03, 25.4) * mm});
            skLineSegment(sketch, "E7.10.6.1", {"start": v(237.23, 25.4) * mm, "end": v(262.63, 50.8) * mm});
            skLineSegment(sketch, "E7.10.6.2", {"start": v(262.63, 0) * mm, "end": v(237.23, 25.4) * mm});
            skLineSegment(sketch, "E7.10.6.3", {"start": v(288.03, 25.4) * mm, "end": v(262.63, 0) * mm});
            skLineSegment(sketch, "E7.10.7.0", {"start": v(262.63, 127) * mm, "end": v(288.03, 101.6) * mm});
            skLineSegment(sketch, "E7.10.7.1", {"start": v(237.23, 101.6) * mm, "end": v(262.63, 127) * mm});
            skLineSegment(sketch, "E7.10.7.2", {"start": v(262.63, 76.2) * mm, "end": v(237.23, 101.6) * mm});
            skLineSegment(sketch, "E7.10.7.3", {"start": v(288.03, 101.6) * mm, "end": v(262.63, 76.2) * mm});
            skLineSegment(sketch, "E7.10.8.0", {"start": v(262.63, 203.2) * mm, "end": v(288.03, 177.8) * mm});
            skLineSegment(sketch, "E7.10.8.1", {"start": v(237.23, 177.8) * mm, "end": v(262.63, 203.2) * mm});
            skLineSegment(sketch, "E7.10.8.2", {"start": v(262.63, 152.4) * mm, "end": v(237.23, 177.8) * mm});
            skLineSegment(sketch, "E7.10.8.3", {"start": v(288.03, 177.8) * mm, "end": v(262.63, 152.4) * mm});
            skLineSegment(sketch, "E7.10.9.0", {"start": v(262.63, 279.4) * mm, "end": v(288.03, 254) * mm});
            skLineSegment(sketch, "E7.10.9.1", {"start": v(237.23, 254) * mm, "end": v(262.63, 279.4) * mm});
            skLineSegment(sketch, "E7.10.9.2", {"start": v(262.63, 228.6) * mm, "end": v(237.23, 254) * mm});
            skLineSegment(sketch, "E7.10.9.3", {"start": v(288.03, 254) * mm, "end": v(262.63, 228.6) * mm});
            skLineSegment(sketch, "E7.10.10.0", {"start": v(262.63, 355.6) * mm, "end": v(288.03, 330.2) * mm});
            skLineSegment(sketch, "E7.10.10.1", {"start": v(237.23, 330.2) * mm, "end": v(262.63, 355.6) * mm});
            skLineSegment(sketch, "E7.10.10.2", {"start": v(262.63, 304.8) * mm, "end": v(237.23, 330.2) * mm});
            skLineSegment(sketch, "E7.10.10.3", {"start": v(288.03, 330.2) * mm, "end": v(262.63, 304.8) * mm});
            skLineSegment(sketch, "E7.10.11.0", {"start": v(262.63, 431.8) * mm, "end": v(288.03, 406.4) * mm});
            skLineSegment(sketch, "E7.10.11.1", {"start": v(237.23, 406.4) * mm, "end": v(262.63, 431.8) * mm});
            skLineSegment(sketch, "E7.10.11.2", {"start": v(262.63, 381) * mm, "end": v(237.23, 406.4) * mm});
            skLineSegment(sketch, "E7.10.11.3", {"start": v(288.03, 406.4) * mm, "end": v(262.63, 381) * mm});
            skLineSegment(sketch, "E7.11.0.0", {"start": v(338.83, -406.4) * mm, "end": v(364.23, -431.8) * mm});
            skLineSegment(sketch, "E7.11.0.1", {"start": v(313.43, -431.8) * mm, "end": v(338.83, -406.4) * mm});
            skLineSegment(sketch, "E7.11.0.2", {"start": v(338.83, -457.2) * mm, "end": v(313.43, -431.8) * mm});
            skLineSegment(sketch, "E7.11.0.3", {"start": v(364.23, -431.8) * mm, "end": v(338.83, -457.2) * mm});
            skLineSegment(sketch, "E7.11.1.0", {"start": v(338.83, -330.2) * mm, "end": v(364.23, -355.6) * mm});
            skLineSegment(sketch, "E7.11.1.1", {"start": v(313.43, -355.6) * mm, "end": v(338.83, -330.2) * mm});
            skLineSegment(sketch, "E7.11.1.2", {"start": v(338.83, -381) * mm, "end": v(313.43, -355.6) * mm});
            skLineSegment(sketch, "E7.11.1.3", {"start": v(364.23, -355.6) * mm, "end": v(338.83, -381) * mm});
            skLineSegment(sketch, "E7.11.2.0", {"start": v(338.83, -254) * mm, "end": v(364.23, -279.4) * mm});
            skLineSegment(sketch, "E7.11.2.1", {"start": v(313.43, -279.4) * mm, "end": v(338.83, -254) * mm});
            skLineSegment(sketch, "E7.11.2.2", {"start": v(338.83, -304.8) * mm, "end": v(313.43, -279.4) * mm});
            skLineSegment(sketch, "E7.11.2.3", {"start": v(364.23, -279.4) * mm, "end": v(338.83, -304.8) * mm});
            skLineSegment(sketch, "E7.11.3.0", {"start": v(338.83, -177.8) * mm, "end": v(364.23, -203.2) * mm});
            skLineSegment(sketch, "E7.11.3.1", {"start": v(313.43, -203.2) * mm, "end": v(338.83, -177.8) * mm});
            skLineSegment(sketch, "E7.11.3.2", {"start": v(338.83, -228.6) * mm, "end": v(313.43, -203.2) * mm});
            skLineSegment(sketch, "E7.11.3.3", {"start": v(364.23, -203.2) * mm, "end": v(338.83, -228.6) * mm});
            skLineSegment(sketch, "E7.11.4.0", {"start": v(338.83, -101.6) * mm, "end": v(364.23, -127) * mm});
            skLineSegment(sketch, "E7.11.4.1", {"start": v(313.43, -127) * mm, "end": v(338.83, -101.6) * mm});
            skLineSegment(sketch, "E7.11.4.2", {"start": v(338.83, -152.4) * mm, "end": v(313.43, -127) * mm});
            skLineSegment(sketch, "E7.11.4.3", {"start": v(364.23, -127) * mm, "end": v(338.83, -152.4) * mm});
            skLineSegment(sketch, "E7.11.5.0", {"start": v(338.83, -25.4) * mm, "end": v(364.23, -50.8) * mm});
            skLineSegment(sketch, "E7.11.5.1", {"start": v(313.43, -50.8) * mm, "end": v(338.83, -25.4) * mm});
            skLineSegment(sketch, "E7.11.5.2", {"start": v(338.83, -76.2) * mm, "end": v(313.43, -50.8) * mm});
            skLineSegment(sketch, "E7.11.5.3", {"start": v(364.23, -50.8) * mm, "end": v(338.83, -76.2) * mm});
            skLineSegment(sketch, "E7.11.6.0", {"start": v(338.83, 50.8) * mm, "end": v(364.23, 25.4) * mm});
            skLineSegment(sketch, "E7.11.6.1", {"start": v(313.43, 25.4) * mm, "end": v(338.83, 50.8) * mm});
            skLineSegment(sketch, "E7.11.6.2", {"start": v(338.83, 0) * mm, "end": v(313.43, 25.4) * mm});
            skLineSegment(sketch, "E7.11.6.3", {"start": v(364.23, 25.4) * mm, "end": v(338.83, 0) * mm});
            skLineSegment(sketch, "E7.11.7.0", {"start": v(338.83, 127) * mm, "end": v(364.23, 101.6) * mm});
            skLineSegment(sketch, "E7.11.7.1", {"start": v(313.43, 101.6) * mm, "end": v(338.83, 127) * mm});
            skLineSegment(sketch, "E7.11.7.2", {"start": v(338.83, 76.2) * mm, "end": v(313.43, 101.6) * mm});
            skLineSegment(sketch, "E7.11.7.3", {"start": v(364.23, 101.6) * mm, "end": v(338.83, 76.2) * mm});
            skLineSegment(sketch, "E7.11.8.0", {"start": v(338.83, 203.2) * mm, "end": v(364.23, 177.8) * mm});
            skLineSegment(sketch, "E7.11.8.1", {"start": v(313.43, 177.8) * mm, "end": v(338.83, 203.2) * mm});
            skLineSegment(sketch, "E7.11.8.2", {"start": v(338.83, 152.4) * mm, "end": v(313.43, 177.8) * mm});
            skLineSegment(sketch, "E7.11.8.3", {"start": v(364.23, 177.8) * mm, "end": v(338.83, 152.4) * mm});
            skLineSegment(sketch, "E7.11.9.0", {"start": v(338.83, 279.4) * mm, "end": v(364.23, 254) * mm});
            skLineSegment(sketch, "E7.11.9.1", {"start": v(313.43, 254) * mm, "end": v(338.83, 279.4) * mm});
            skLineSegment(sketch, "E7.11.9.2", {"start": v(338.83, 228.6) * mm, "end": v(313.43, 254) * mm});
            skLineSegment(sketch, "E7.11.9.3", {"start": v(364.23, 254) * mm, "end": v(338.83, 228.6) * mm});
            skLineSegment(sketch, "E7.11.10.0", {"start": v(338.83, 355.6) * mm, "end": v(364.23, 330.2) * mm});
            skLineSegment(sketch, "E7.11.10.1", {"start": v(313.43, 330.2) * mm, "end": v(338.83, 355.6) * mm});
            skLineSegment(sketch, "E7.11.10.2", {"start": v(338.83, 304.8) * mm, "end": v(313.43, 330.2) * mm});
            skLineSegment(sketch, "E7.11.10.3", {"start": v(364.23, 330.2) * mm, "end": v(338.83, 304.8) * mm});
            skLineSegment(sketch, "E7.11.11.0", {"start": v(338.83, 431.8) * mm, "end": v(364.23, 406.4) * mm});
            skLineSegment(sketch, "E7.11.11.1", {"start": v(313.43, 406.4) * mm, "end": v(338.83, 431.8) * mm});
            skLineSegment(sketch, "E7.11.11.2", {"start": v(338.83, 381) * mm, "end": v(313.43, 406.4) * mm});
            skLineSegment(sketch, "E7.11.11.3", {"start": v(364.23, 406.4) * mm, "end": v(338.83, 381) * mm});
            skLineSegment(sketch, "E7.12.0.0", {"start": v(415.03, -406.4) * mm, "end": v(440.43, -431.8) * mm});
            skLineSegment(sketch, "E7.12.0.1", {"start": v(389.63, -431.8) * mm, "end": v(415.03, -406.4) * mm});
            skLineSegment(sketch, "E7.12.0.2", {"start": v(415.03, -457.2) * mm, "end": v(389.63, -431.8) * mm});
            skLineSegment(sketch, "E7.12.0.3", {"start": v(440.43, -431.8) * mm, "end": v(415.03, -457.2) * mm});
            skLineSegment(sketch, "E7.12.1.0", {"start": v(415.03, -330.2) * mm, "end": v(440.43, -355.6) * mm});
            skLineSegment(sketch, "E7.12.1.1", {"start": v(389.63, -355.6) * mm, "end": v(415.03, -330.2) * mm});
            skLineSegment(sketch, "E7.12.1.2", {"start": v(415.03, -381) * mm, "end": v(389.63, -355.6) * mm});
            skLineSegment(sketch, "E7.12.1.3", {"start": v(440.43, -355.6) * mm, "end": v(415.03, -381) * mm});
            skLineSegment(sketch, "E7.12.2.0", {"start": v(415.03, -254) * mm, "end": v(440.43, -279.4) * mm});
            skLineSegment(sketch, "E7.12.2.1", {"start": v(389.63, -279.4) * mm, "end": v(415.03, -254) * mm});
            skLineSegment(sketch, "E7.12.2.2", {"start": v(415.03, -304.8) * mm, "end": v(389.63, -279.4) * mm});
            skLineSegment(sketch, "E7.12.2.3", {"start": v(440.43, -279.4) * mm, "end": v(415.03, -304.8) * mm});
            skLineSegment(sketch, "E7.12.3.0", {"start": v(415.03, -177.8) * mm, "end": v(440.43, -203.2) * mm});
            skLineSegment(sketch, "E7.12.3.1", {"start": v(389.63, -203.2) * mm, "end": v(415.03, -177.8) * mm});
            skLineSegment(sketch, "E7.12.3.2", {"start": v(415.03, -228.6) * mm, "end": v(389.63, -203.2) * mm});
            skLineSegment(sketch, "E7.12.3.3", {"start": v(440.43, -203.2) * mm, "end": v(415.03, -228.6) * mm});
            skLineSegment(sketch, "E7.12.4.0", {"start": v(415.03, -101.6) * mm, "end": v(440.43, -127) * mm});
            skLineSegment(sketch, "E7.12.4.1", {"start": v(389.63, -127) * mm, "end": v(415.03, -101.6) * mm});
            skLineSegment(sketch, "E7.12.4.2", {"start": v(415.03, -152.4) * mm, "end": v(389.63, -127) * mm});
            skLineSegment(sketch, "E7.12.4.3", {"start": v(440.43, -127) * mm, "end": v(415.03, -152.4) * mm});
            skLineSegment(sketch, "E7.12.5.0", {"start": v(415.03, -25.4) * mm, "end": v(440.43, -50.8) * mm});
            skLineSegment(sketch, "E7.12.5.1", {"start": v(389.63, -50.8) * mm, "end": v(415.03, -25.4) * mm});
            skLineSegment(sketch, "E7.12.5.2", {"start": v(415.03, -76.2) * mm, "end": v(389.63, -50.8) * mm});
            skLineSegment(sketch, "E7.12.5.3", {"start": v(440.43, -50.8) * mm, "end": v(415.03, -76.2) * mm});
            skLineSegment(sketch, "E7.12.6.0", {"start": v(415.03, 50.8) * mm, "end": v(440.43, 25.4) * mm});
            skLineSegment(sketch, "E7.12.6.1", {"start": v(389.63, 25.4) * mm, "end": v(415.03, 50.8) * mm});
            skLineSegment(sketch, "E7.12.6.2", {"start": v(415.03, 0) * mm, "end": v(389.63, 25.4) * mm});
            skLineSegment(sketch, "E7.12.6.3", {"start": v(440.43, 25.4) * mm, "end": v(415.03, 0) * mm});
            skLineSegment(sketch, "E7.12.7.0", {"start": v(415.03, 127) * mm, "end": v(440.43, 101.6) * mm});
            skLineSegment(sketch, "E7.12.7.1", {"start": v(389.63, 101.6) * mm, "end": v(415.03, 127) * mm});
            skLineSegment(sketch, "E7.12.7.2", {"start": v(415.03, 76.2) * mm, "end": v(389.63, 101.6) * mm});
            skLineSegment(sketch, "E7.12.7.3", {"start": v(440.43, 101.6) * mm, "end": v(415.03, 76.2) * mm});
            skLineSegment(sketch, "E7.12.8.0", {"start": v(415.03, 203.2) * mm, "end": v(440.43, 177.8) * mm});
            skLineSegment(sketch, "E7.12.8.1", {"start": v(389.63, 177.8) * mm, "end": v(415.03, 203.2) * mm});
            skLineSegment(sketch, "E7.12.8.2", {"start": v(415.03, 152.4) * mm, "end": v(389.63, 177.8) * mm});
            skLineSegment(sketch, "E7.12.8.3", {"start": v(440.43, 177.8) * mm, "end": v(415.03, 152.4) * mm});
            skLineSegment(sketch, "E7.12.9.0", {"start": v(415.03, 279.4) * mm, "end": v(440.43, 254) * mm});
            skLineSegment(sketch, "E7.12.9.1", {"start": v(389.63, 254) * mm, "end": v(415.03, 279.4) * mm});
            skLineSegment(sketch, "E7.12.9.2", {"start": v(415.03, 228.6) * mm, "end": v(389.63, 254) * mm});
            skLineSegment(sketch, "E7.12.9.3", {"start": v(440.43, 254) * mm, "end": v(415.03, 228.6) * mm});
            skLineSegment(sketch, "E7.12.10.0", {"start": v(415.03, 355.6) * mm, "end": v(440.43, 330.2) * mm});
            skLineSegment(sketch, "E7.12.10.1", {"start": v(389.63, 330.2) * mm, "end": v(415.03, 355.6) * mm});
            skLineSegment(sketch, "E7.12.10.2", {"start": v(415.03, 304.8) * mm, "end": v(389.63, 330.2) * mm});
            skLineSegment(sketch, "E7.12.10.3", {"start": v(440.43, 330.2) * mm, "end": v(415.03, 304.8) * mm});
            skLineSegment(sketch, "E7.12.11.0", {"start": v(415.03, 431.8) * mm, "end": v(440.43, 406.4) * mm});
            skLineSegment(sketch, "E7.12.11.1", {"start": v(389.63, 406.4) * mm, "end": v(415.03, 431.8) * mm});
            skLineSegment(sketch, "E7.12.11.2", {"start": v(415.03, 381) * mm, "end": v(389.63, 406.4) * mm});
            skLineSegment(sketch, "E7.12.11.3", {"start": v(440.43, 406.4) * mm, "end": v(415.03, 381) * mm});
            skLineSegment(sketch, "E7.13.0.0", {"start": v(491.23, -406.4) * mm, "end": v(516.63, -431.8) * mm});
            skLineSegment(sketch, "E7.13.0.1", {"start": v(465.83, -431.8) * mm, "end": v(491.23, -406.4) * mm});
            skLineSegment(sketch, "E7.13.0.2", {"start": v(491.23, -457.2) * mm, "end": v(465.83, -431.8) * mm});
            skLineSegment(sketch, "E7.13.0.3", {"start": v(516.63, -431.8) * mm, "end": v(491.23, -457.2) * mm});
            skLineSegment(sketch, "E7.13.1.0", {"start": v(491.23, -330.2) * mm, "end": v(516.63, -355.6) * mm});
            skLineSegment(sketch, "E7.13.1.1", {"start": v(465.83, -355.6) * mm, "end": v(491.23, -330.2) * mm});
            skLineSegment(sketch, "E7.13.1.2", {"start": v(491.23, -381) * mm, "end": v(465.83, -355.6) * mm});
            skLineSegment(sketch, "E7.13.1.3", {"start": v(516.63, -355.6) * mm, "end": v(491.23, -381) * mm});
            skLineSegment(sketch, "E7.13.2.0", {"start": v(491.23, -254) * mm, "end": v(516.63, -279.4) * mm});
            skLineSegment(sketch, "E7.13.2.1", {"start": v(465.83, -279.4) * mm, "end": v(491.23, -254) * mm});
            skLineSegment(sketch, "E7.13.2.2", {"start": v(491.23, -304.8) * mm, "end": v(465.83, -279.4) * mm});
            skLineSegment(sketch, "E7.13.2.3", {"start": v(516.63, -279.4) * mm, "end": v(491.23, -304.8) * mm});
            skLineSegment(sketch, "E7.13.3.0", {"start": v(491.23, -177.8) * mm, "end": v(516.63, -203.2) * mm});
            skLineSegment(sketch, "E7.13.3.1", {"start": v(465.83, -203.2) * mm, "end": v(491.23, -177.8) * mm});
            skLineSegment(sketch, "E7.13.3.2", {"start": v(491.23, -228.6) * mm, "end": v(465.83, -203.2) * mm});
            skLineSegment(sketch, "E7.13.3.3", {"start": v(516.63, -203.2) * mm, "end": v(491.23, -228.6) * mm});
            skLineSegment(sketch, "E7.13.4.0", {"start": v(491.23, -101.6) * mm, "end": v(516.63, -127) * mm});
            skLineSegment(sketch, "E7.13.4.1", {"start": v(465.83, -127) * mm, "end": v(491.23, -101.6) * mm});
            skLineSegment(sketch, "E7.13.4.2", {"start": v(491.23, -152.4) * mm, "end": v(465.83, -127) * mm});
            skLineSegment(sketch, "E7.13.4.3", {"start": v(516.63, -127) * mm, "end": v(491.23, -152.4) * mm});
            skLineSegment(sketch, "E7.13.5.0", {"start": v(491.23, -25.4) * mm, "end": v(516.63, -50.8) * mm});
            skLineSegment(sketch, "E7.13.5.1", {"start": v(465.83, -50.8) * mm, "end": v(491.23, -25.4) * mm});
            skLineSegment(sketch, "E7.13.5.2", {"start": v(491.23, -76.2) * mm, "end": v(465.83, -50.8) * mm});
            skLineSegment(sketch, "E7.13.5.3", {"start": v(516.63, -50.8) * mm, "end": v(491.23, -76.2) * mm});
            skLineSegment(sketch, "E7.13.6.0", {"start": v(491.23, 50.8) * mm, "end": v(516.63, 25.4) * mm});
            skLineSegment(sketch, "E7.13.6.1", {"start": v(465.83, 25.4) * mm, "end": v(491.23, 50.8) * mm});
            skLineSegment(sketch, "E7.13.6.2", {"start": v(491.23, 0) * mm, "end": v(465.83, 25.4) * mm});
            skLineSegment(sketch, "E7.13.6.3", {"start": v(516.63, 25.4) * mm, "end": v(491.23, 0) * mm});
            skLineSegment(sketch, "E7.13.7.0", {"start": v(491.23, 127) * mm, "end": v(516.63, 101.6) * mm});
            skLineSegment(sketch, "E7.13.7.1", {"start": v(465.83, 101.6) * mm, "end": v(491.23, 127) * mm});
            skLineSegment(sketch, "E7.13.7.2", {"start": v(491.23, 76.2) * mm, "end": v(465.83, 101.6) * mm});
            skLineSegment(sketch, "E7.13.7.3", {"start": v(516.63, 101.6) * mm, "end": v(491.23, 76.2) * mm});
            skLineSegment(sketch, "E7.13.8.0", {"start": v(491.23, 203.2) * mm, "end": v(516.63, 177.8) * mm});
            skLineSegment(sketch, "E7.13.8.1", {"start": v(465.83, 177.8) * mm, "end": v(491.23, 203.2) * mm});
            skLineSegment(sketch, "E7.13.8.2", {"start": v(491.23, 152.4) * mm, "end": v(465.83, 177.8) * mm});
            skLineSegment(sketch, "E7.13.8.3", {"start": v(516.63, 177.8) * mm, "end": v(491.23, 152.4) * mm});
            skLineSegment(sketch, "E7.13.9.0", {"start": v(491.23, 279.4) * mm, "end": v(516.63, 254) * mm});
            skLineSegment(sketch, "E7.13.9.1", {"start": v(465.83, 254) * mm, "end": v(491.23, 279.4) * mm});
            skLineSegment(sketch, "E7.13.9.2", {"start": v(491.23, 228.6) * mm, "end": v(465.83, 254) * mm});
            skLineSegment(sketch, "E7.13.9.3", {"start": v(516.63, 254) * mm, "end": v(491.23, 228.6) * mm});
            skLineSegment(sketch, "E7.13.10.0", {"start": v(491.23, 355.6) * mm, "end": v(516.63, 330.2) * mm});
            skLineSegment(sketch, "E7.13.10.1", {"start": v(465.83, 330.2) * mm, "end": v(491.23, 355.6) * mm});
            skLineSegment(sketch, "E7.13.10.2", {"start": v(491.23, 304.8) * mm, "end": v(465.83, 330.2) * mm});
            skLineSegment(sketch, "E7.13.10.3", {"start": v(516.63, 330.2) * mm, "end": v(491.23, 304.8) * mm});
            skLineSegment(sketch, "E7.13.11.0", {"start": v(491.23, 431.8) * mm, "end": v(516.63, 406.4) * mm});
            skLineSegment(sketch, "E7.13.11.1", {"start": v(465.83, 406.4) * mm, "end": v(491.23, 431.8) * mm});
            skLineSegment(sketch, "E7.13.11.2", {"start": v(491.23, 381) * mm, "end": v(465.83, 406.4) * mm});
            skLineSegment(sketch, "E7.13.11.3", {"start": v(516.63, 406.4) * mm, "end": v(491.23, 381) * mm});
            skLineSegment(sketch, "E7.14.0.0", {"start": v(567.43, -406.4) * mm, "end": v(592.83, -431.8) * mm});
            skLineSegment(sketch, "E7.14.0.1", {"start": v(542.03, -431.8) * mm, "end": v(567.43, -406.4) * mm});
            skLineSegment(sketch, "E7.14.0.2", {"start": v(567.43, -457.2) * mm, "end": v(542.03, -431.8) * mm});
            skLineSegment(sketch, "E7.14.0.3", {"start": v(592.83, -431.8) * mm, "end": v(567.43, -457.2) * mm});
            skLineSegment(sketch, "E7.14.1.0", {"start": v(567.43, -330.2) * mm, "end": v(592.83, -355.6) * mm});
            skLineSegment(sketch, "E7.14.1.1", {"start": v(542.03, -355.6) * mm, "end": v(567.43, -330.2) * mm});
            skLineSegment(sketch, "E7.14.1.2", {"start": v(567.43, -381) * mm, "end": v(542.03, -355.6) * mm});
            skLineSegment(sketch, "E7.14.1.3", {"start": v(592.83, -355.6) * mm, "end": v(567.43, -381) * mm});
            skLineSegment(sketch, "E7.14.2.0", {"start": v(567.43, -254) * mm, "end": v(592.83, -279.4) * mm});
            skLineSegment(sketch, "E7.14.2.1", {"start": v(542.03, -279.4) * mm, "end": v(567.43, -254) * mm});
            skLineSegment(sketch, "E7.14.2.2", {"start": v(567.43, -304.8) * mm, "end": v(542.03, -279.4) * mm});
            skLineSegment(sketch, "E7.14.2.3", {"start": v(592.83, -279.4) * mm, "end": v(567.43, -304.8) * mm});
            skLineSegment(sketch, "E7.14.3.0", {"start": v(567.43, -177.8) * mm, "end": v(592.83, -203.2) * mm});
            skLineSegment(sketch, "E7.14.3.1", {"start": v(542.03, -203.2) * mm, "end": v(567.43, -177.8) * mm});
            skLineSegment(sketch, "E7.14.3.2", {"start": v(567.43, -228.6) * mm, "end": v(542.03, -203.2) * mm});
            skLineSegment(sketch, "E7.14.3.3", {"start": v(592.83, -203.2) * mm, "end": v(567.43, -228.6) * mm});
            skLineSegment(sketch, "E7.14.4.0", {"start": v(567.43, -101.6) * mm, "end": v(592.83, -127) * mm});
            skLineSegment(sketch, "E7.14.4.1", {"start": v(542.03, -127) * mm, "end": v(567.43, -101.6) * mm});
            skLineSegment(sketch, "E7.14.4.2", {"start": v(567.43, -152.4) * mm, "end": v(542.03, -127) * mm});
            skLineSegment(sketch, "E7.14.4.3", {"start": v(592.83, -127) * mm, "end": v(567.43, -152.4) * mm});
            skLineSegment(sketch, "E7.14.5.0", {"start": v(567.43, -25.4) * mm, "end": v(592.83, -50.8) * mm});
            skLineSegment(sketch, "E7.14.5.1", {"start": v(542.03, -50.8) * mm, "end": v(567.43, -25.4) * mm});
            skLineSegment(sketch, "E7.14.5.2", {"start": v(567.43, -76.2) * mm, "end": v(542.03, -50.8) * mm});
            skLineSegment(sketch, "E7.14.5.3", {"start": v(592.83, -50.8) * mm, "end": v(567.43, -76.2) * mm});
            skLineSegment(sketch, "E7.14.6.0", {"start": v(567.43, 50.8) * mm, "end": v(592.83, 25.4) * mm});
            skLineSegment(sketch, "E7.14.6.1", {"start": v(542.03, 25.4) * mm, "end": v(567.43, 50.8) * mm});
            skLineSegment(sketch, "E7.14.6.2", {"start": v(567.43, 0) * mm, "end": v(542.03, 25.4) * mm});
            skLineSegment(sketch, "E7.14.6.3", {"start": v(592.83, 25.4) * mm, "end": v(567.43, 0) * mm});
            skLineSegment(sketch, "E7.14.7.0", {"start": v(567.43, 127) * mm, "end": v(592.83, 101.6) * mm});
            skLineSegment(sketch, "E7.14.7.1", {"start": v(542.03, 101.6) * mm, "end": v(567.43, 127) * mm});
            skLineSegment(sketch, "E7.14.7.2", {"start": v(567.43, 76.2) * mm, "end": v(542.03, 101.6) * mm});
            skLineSegment(sketch, "E7.14.7.3", {"start": v(592.83, 101.6) * mm, "end": v(567.43, 76.2) * mm});
            skLineSegment(sketch, "E7.14.8.0", {"start": v(567.43, 203.2) * mm, "end": v(592.83, 177.8) * mm});
            skLineSegment(sketch, "E7.14.8.1", {"start": v(542.03, 177.8) * mm, "end": v(567.43, 203.2) * mm});
            skLineSegment(sketch, "E7.14.8.2", {"start": v(567.43, 152.4) * mm, "end": v(542.03, 177.8) * mm});
            skLineSegment(sketch, "E7.14.8.3", {"start": v(592.83, 177.8) * mm, "end": v(567.43, 152.4) * mm});
            skLineSegment(sketch, "E7.14.9.0", {"start": v(567.43, 279.4) * mm, "end": v(592.83, 254) * mm});
            skLineSegment(sketch, "E7.14.9.1", {"start": v(542.03, 254) * mm, "end": v(567.43, 279.4) * mm});
            skLineSegment(sketch, "E7.14.9.2", {"start": v(567.43, 228.6) * mm, "end": v(542.03, 254) * mm});
            skLineSegment(sketch, "E7.14.9.3", {"start": v(592.83, 254) * mm, "end": v(567.43, 228.6) * mm});
            skLineSegment(sketch, "E7.14.10.0", {"start": v(567.43, 355.6) * mm, "end": v(592.83, 330.2) * mm});
            skLineSegment(sketch, "E7.14.10.1", {"start": v(542.03, 330.2) * mm, "end": v(567.43, 355.6) * mm});
            skLineSegment(sketch, "E7.14.10.2", {"start": v(567.43, 304.8) * mm, "end": v(542.03, 330.2) * mm});
            skLineSegment(sketch, "E7.14.10.3", {"start": v(592.83, 330.2) * mm, "end": v(567.43, 304.8) * mm});
            skLineSegment(sketch, "E7.14.11.0", {"start": v(567.43, 431.8) * mm, "end": v(592.83, 406.4) * mm});
            skLineSegment(sketch, "E7.14.11.1", {"start": v(542.03, 406.4) * mm, "end": v(567.43, 431.8) * mm});
            skLineSegment(sketch, "E7.14.11.2", {"start": v(567.43, 381) * mm, "end": v(542.03, 406.4) * mm});
            skLineSegment(sketch, "E7.14.11.3", {"start": v(592.83, 406.4) * mm, "end": v(567.43, 381) * mm});
            skLineSegment(sketch, "E7.direction1", {"start": v(-499.37, -457.2) * mm, "end": v(-423.17, -457.2) * mm, "construction": true});
            skLineSegment(sketch, "E7.direction2", {"start": v(-499.37, -457.2) * mm, "end": v(-499.37, -381) * mm, "construction": true});
            skSolve(sketch);
        }
        {
            var Q0;
            Q0 = qSketchRegion(id + "F2", true);
            extrude(context, id + "F3", {"entities" : qUnion([Q0]), "operationType" : NewBodyOperationType.REMOVE, "endBound" : BoundingType.THROUGH_ALL, "oppositeDirection" : true, "depth" : 25.4 * mm});
        }
        {
            var Q0;
            Q0=makeQuery(id+"F1.opExtrude","CAP_FACE",FACE,{"disambiguationData":[OSD([sQuery(id+"F0.wireOp",EDGE,"E0.bottom"),sQuery(id+"F0.wireOp",EDGE,"E0.top"),sQuery(id+"F0.wireOp",EDGE,"E0.left"),sQuery(id+"F0.wireOp",EDGE,"E0.right")])],"isStart":false});
            var sketch = newSketch(context, id + "F4", { "sketchPlane" : qUnion([Q0])});
            skLineSegment(sketch, "E8.bottom", {"start": v(-575.57, -508) * mm, "end": v(-372.37, -508) * mm});
            skLineSegment(sketch, "E8.top", {"start": v(-575.57, -368.3) * mm, "end": v(-372.37, -368.3) * mm});
            skLineSegment(sketch, "E8.left", {"start": v(-575.57, -508) * mm, "end": v(-575.57, -368.3) * mm});
            skLineSegment(sketch, "E8.right", {"start": v(-372.37, -508) * mm, "end": v(-372.37, -368.3) * mm});
            skLineSegment(sketch, "E9.0.1.0", {"start": v(-575.57, 69.85) * mm, "end": v(-372.37, 69.85) * mm});
            skLineSegment(sketch, "E9.0.1.1", {"start": v(-575.57, -69.85) * mm, "end": v(-575.57, 69.85) * mm});
            skLineSegment(sketch, "E9.0.1.2", {"start": v(-575.57, -69.85) * mm, "end": v(-372.37, -69.85) * mm});
            skLineSegment(sketch, "E9.0.1.3", {"start": v(-372.37, -69.85) * mm, "end": v(-372.37, 69.85) * mm});
            skLineSegment(sketch, "E9.0.2.0", {"start": v(-575.57, 508) * mm, "end": v(-372.37, 508) * mm});
            skLineSegment(sketch, "E9.0.2.1", {"start": v(-575.57, 368.3) * mm, "end": v(-575.57, 508) * mm});
            skLineSegment(sketch, "E9.0.2.2", {"start": v(-575.57, 368.3) * mm, "end": v(-372.37, 368.3) * mm});
            skLineSegment(sketch, "E9.0.2.3", {"start": v(-372.37, 368.3) * mm, "end": v(-372.37, 508) * mm});
            skLineSegment(sketch, "E9.1.0.0", {"start": v(-67.57, -368.3) * mm, "end": v(135.63, -368.3) * mm});
            skLineSegment(sketch, "E9.1.0.1", {"start": v(-67.57, -508) * mm, "end": v(-67.57, -368.3) * mm});
            skLineSegment(sketch, "E9.1.0.2", {"start": v(-67.57, -508) * mm, "end": v(135.63, -508) * mm});
            skLineSegment(sketch, "E9.1.0.3", {"start": v(135.63, -508) * mm, "end": v(135.63, -368.3) * mm});
            skLineSegment(sketch, "E9.1.1.0", {"start": v(-67.57, 69.85) * mm, "end": v(135.63, 69.85) * mm});
            skLineSegment(sketch, "E9.1.1.1", {"start": v(-67.57, -69.85) * mm, "end": v(-67.57, 69.85) * mm});
            skLineSegment(sketch, "E9.1.1.2", {"start": v(-67.57, -69.85) * mm, "end": v(135.63, -69.85) * mm});
            skLineSegment(sketch, "E9.1.1.3", {"start": v(135.63, -69.85) * mm, "end": v(135.63, 69.85) * mm});
            skLineSegment(sketch, "E9.1.2.0", {"start": v(-67.57, 508) * mm, "end": v(135.63, 508) * mm});
            skLineSegment(sketch, "E9.1.2.1", {"start": v(-67.57, 368.3) * mm, "end": v(-67.57, 508) * mm});
            skLineSegment(sketch, "E9.1.2.2", {"start": v(-67.57, 368.3) * mm, "end": v(135.63, 368.3) * mm});
            skLineSegment(sketch, "E9.1.2.3", {"start": v(135.63, 368.3) * mm, "end": v(135.63, 508) * mm});
            skLineSegment(sketch, "E9.2.0.0", {"start": v(440.43, -368.3) * mm, "end": v(643.63, -368.3) * mm});
            skLineSegment(sketch, "E9.2.0.1", {"start": v(440.43, -508) * mm, "end": v(440.43, -368.3) * mm});
            skLineSegment(sketch, "E9.2.0.2", {"start": v(440.43, -508) * mm, "end": v(643.63, -508) * mm});
            skLineSegment(sketch, "E9.2.0.3", {"start": v(643.63, -508) * mm, "end": v(643.63, -368.3) * mm});
            skLineSegment(sketch, "E9.2.1.0", {"start": v(440.43, 69.85) * mm, "end": v(643.63, 69.85) * mm});
            skLineSegment(sketch, "E9.2.1.1", {"start": v(440.43, -69.85) * mm, "end": v(440.43, 69.85) * mm});
            skLineSegment(sketch, "E9.2.1.2", {"start": v(440.43, -69.85) * mm, "end": v(643.63, -69.85) * mm});
            skLineSegment(sketch, "E9.2.1.3", {"start": v(643.63, -69.85) * mm, "end": v(643.63, 69.85) * mm});
            skLineSegment(sketch, "E9.2.2.0", {"start": v(440.43, 508) * mm, "end": v(643.63, 508) * mm});
            skLineSegment(sketch, "E9.2.2.1", {"start": v(440.43, 368.3) * mm, "end": v(440.43, 508) * mm});
            skLineSegment(sketch, "E9.2.2.2", {"start": v(440.43, 368.3) * mm, "end": v(643.63, 368.3) * mm});
            skLineSegment(sketch, "E9.2.2.3", {"start": v(643.63, 368.3) * mm, "end": v(643.63, 508) * mm});
            skLineSegment(sketch, "E9.direction1", {"start": v(-575.57, -368.3) * mm, "end": v(-67.57, -368.3) * mm, "construction": true});
            skLineSegment(sketch, "E9.direction2", {"start": v(-575.57, -368.3) * mm, "end": v(-575.57, 69.85) * mm, "construction": true});
            skSolve(sketch);
        }
        {
            var Q0;
            Q0 = qSketchRegion(id + "F4", true);
            extrude(context, id + "F5", {"entities" : qUnion([Q0]), "operationType" : NewBodyOperationType.ADD, "oppositeDirection" : true, "depth" : 139.7 * mm});
        }
    });
